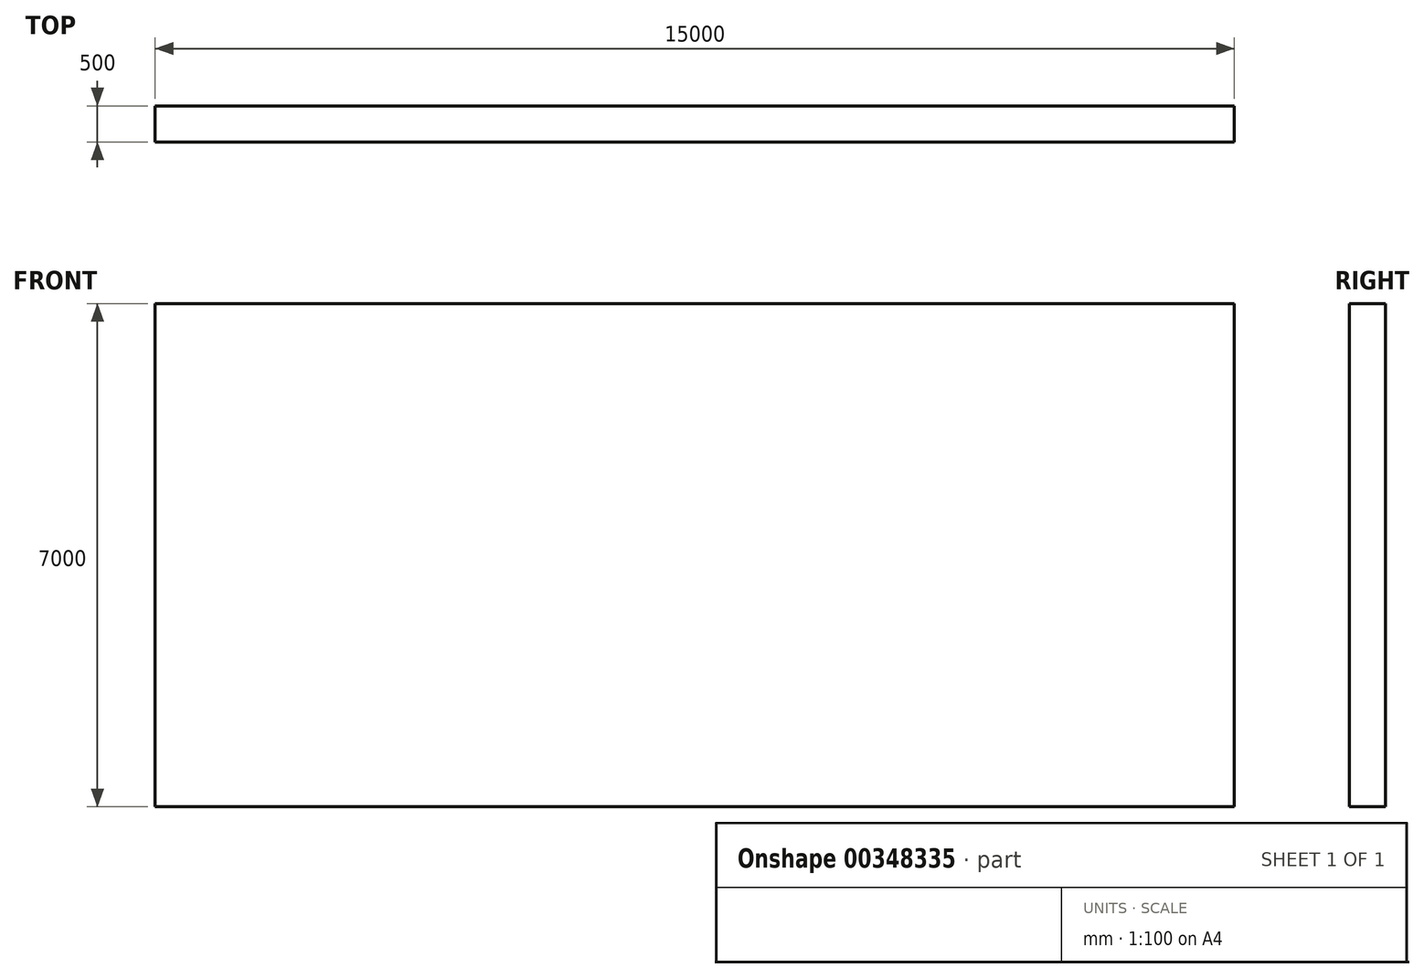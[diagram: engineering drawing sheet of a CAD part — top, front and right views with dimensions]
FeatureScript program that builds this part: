
annotation { "Feature Type Name" : "Feature", "Feature Type Description" : "" }
export const myFeature = defineFeature(function(context is Context, id is Id, definition is map)
    precondition{}
    {
        {
            var Q0;
            Q0=qCreatedBy(makeId("Front.planeOp"),FACE);
            var sketch = newSketch(context, id + "F0", { "sketchPlane" : qUnion([Q0])});
            skLineSegment(sketch, "E0.bottom", {"start": v(7500, 3500) * mm, "end": v(-7500, 3500) * mm});
            skLineSegment(sketch, "E0.top", {"start": v(7500, -3500) * mm, "end": v(-7500, -3500) * mm});
            skLineSegment(sketch, "E0.left", {"start": v(7500, 3500) * mm, "end": v(7500, -3500) * mm});
            skLineSegment(sketch, "E0.right", {"start": v(-7500, 3500) * mm, "end": v(-7500, -3500) * mm});
            skPoint(sketch, "E0.middle", {"position": v(0, 0) * mm});
            skSolve(sketch);
        }
        {
            var Q0;
            Q0=makeQuery(id+"F0.imprint","IMPRINT",FACE,{"disambiguationData":[TD([[makeQuery(id+"F0.imprint","IMPRINT",EDGE,{"derivedFrom":sQuery(id+"F0.wireOp",EDGE,"E0.bottom")}),1.0]])]});
            extrude(context, id + "F1", {"entities" : qUnion([Q0]), "depth" : 500 * mm});
        }
        {
            var Q0;
            Q0=makeQuery(id+"F1.opExtrude","CAP_FACE",FACE,{"disambiguationData":[OSD([sQuery(id+"F0.wireOp",EDGE,"E0.bottom"),sQuery(id+"F0.wireOp",EDGE,"E0.top"),sQuery(id+"F0.wireOp",EDGE,"E0.left"),sQuery(id+"F0.wireOp",EDGE,"E0.right")])],"isStart":false});
            var sketch = newSketch(context, id + "F2", { "sketchPlane" : qUnion([Q0])});
            skLineSegment(sketch, "E1.MirrorCS", {"start": v(-7500, -3000) * mm, "end": v(7500, -3000) * mm});
            skLineSegment(sketch, "E2", {"start": v(7500, -3500) * mm, "end": v(-7500, -3500) * mm});
            skLineSegment(sketch, "E3.MirrorCS", {"start": v(-1000, -3500) * mm, "end": v(-1000, 3500) * mm});
            skLineSegment(sketch, "E4.0", {"start": v(-7490, -3500) * mm, "end": v(-7490, 3500) * mm});
            skLineSegment(sketch, "E5.0", {"start": v(-6990, -3500) * mm, "end": v(-6990, 3500) * mm});
            skLineSegment(sketch, "E6.MirrorCS", {"start": v(-7010, -3500) * mm, "end": v(-7010, 3500) * mm});
            skLineSegment(sketch, "E7.0", {"start": v(-6490, -3500) * mm, "end": v(-6490, 3500) * mm});
            skLineSegment(sketch, "E8.MirrorCS", {"start": v(-6510, -3500) * mm, "end": v(-6510, 3500) * mm});
            skLineSegment(sketch, "E9.0", {"start": v(-5990, -3500) * mm, "end": v(-5990, 3500) * mm});
            skLineSegment(sketch, "E10.MirrorCS", {"start": v(-6010, -3500) * mm, "end": v(-6010, 3500) * mm});
            skLineSegment(sketch, "E11.0", {"start": v(-5490, -3500) * mm, "end": v(-5490, 3500) * mm});
            skLineSegment(sketch, "E12.MirrorCS", {"start": v(-5510, -3500) * mm, "end": v(-5510, 3500) * mm});
            skLineSegment(sketch, "E13.0", {"start": v(-4990, -3500) * mm, "end": v(-4990, 3500) * mm});
            skLineSegment(sketch, "E14.MirrorCS", {"start": v(-5010, -3500) * mm, "end": v(-5010, 3500) * mm});
            skLineSegment(sketch, "E15.0", {"start": v(-4490, -3500) * mm, "end": v(-4490, 3500) * mm});
            skLineSegment(sketch, "E16.MirrorCS", {"start": v(-4510, -3500) * mm, "end": v(-4510, 3500) * mm});
            skLineSegment(sketch, "E17.0", {"start": v(-3990, -3500) * mm, "end": v(-3990, 3500) * mm});
            skLineSegment(sketch, "E18.MirrorCS", {"start": v(-4010, -3500) * mm, "end": v(-4010, 3500) * mm});
            skLineSegment(sketch, "E19.0", {"start": v(-3490, -3500) * mm, "end": v(-3490, 3500) * mm});
            skLineSegment(sketch, "E20.MirrorCS", {"start": v(-3510, -3500) * mm, "end": v(-3510, 3500) * mm});
            skLineSegment(sketch, "E21.0", {"start": v(-2990, -3500) * mm, "end": v(-2990, 3500) * mm});
            skLineSegment(sketch, "E22.MirrorCS", {"start": v(-3010, -3500) * mm, "end": v(-3010, 3500) * mm});
            skLineSegment(sketch, "E23.0", {"start": v(-2490, -3500) * mm, "end": v(-2490, 3500) * mm});
            skLineSegment(sketch, "E24.MirrorCS", {"start": v(-2510, -3500) * mm, "end": v(-2510, 3500) * mm});
            skLineSegment(sketch, "E25.0", {"start": v(-1990, -3500) * mm, "end": v(-1990, 3500) * mm});
            skLineSegment(sketch, "E26.MirrorCS", {"start": v(-2010, -3500) * mm, "end": v(-2010, 3500) * mm});
            skLineSegment(sketch, "E27.0", {"start": v(-1490, -3500) * mm, "end": v(-1490, 3500) * mm});
            skLineSegment(sketch, "E28.MirrorCS", {"start": v(-1510, -3500) * mm, "end": v(-1510, 3500) * mm});
            skLineSegment(sketch, "E29.MirrorCS", {"start": v(-510, -3500) * mm, "end": v(-510, 3500) * mm});
            skLineSegment(sketch, "E30.MirrorCS", {"start": v(-490, -3500) * mm, "end": v(-490, 3500) * mm});
            skLineSegment(sketch, "E31.MirrorCS", {"start": v(-10, -3500) * mm, "end": v(-10, 3500) * mm});
            skLineSegment(sketch, "E32.MirrorCS", {"start": v(10, -3500) * mm, "end": v(10, 3500) * mm});
            skLineSegment(sketch, "E33.MirrorCS", {"start": v(490, -3500) * mm, "end": v(490, 3500) * mm});
            skLineSegment(sketch, "E34.MirrorCS", {"start": v(510, -3500) * mm, "end": v(510, 3500) * mm});
            skLineSegment(sketch, "E35.MirrorCS", {"start": v(990, -3500) * mm, "end": v(990, 3500) * mm});
            skLineSegment(sketch, "E36.MirrorCS", {"start": v(1010, -3500) * mm, "end": v(1010, 3500) * mm});
            skLineSegment(sketch, "E37.MirrorCS", {"start": v(1490, -3500) * mm, "end": v(1490, 3500) * mm});
            skLineSegment(sketch, "E38.MirrorCS", {"start": v(1510, -3500) * mm, "end": v(1510, 3500) * mm});
            skLineSegment(sketch, "E39.MirrorCS", {"start": v(1990, -3500) * mm, "end": v(1990, 3500) * mm});
            skLineSegment(sketch, "E40.MirrorCS", {"start": v(2010, -3500) * mm, "end": v(2010, 3500) * mm});
            skLineSegment(sketch, "E41.MirrorCS", {"start": v(2490, -3500) * mm, "end": v(2490, 3500) * mm});
            skLineSegment(sketch, "E42.MirrorCS", {"start": v(2510, -3500) * mm, "end": v(2510, 3500) * mm});
            skLineSegment(sketch, "E43.MirrorCS", {"start": v(2990, -3500) * mm, "end": v(2990, 3500) * mm});
            skLineSegment(sketch, "E44.MirrorCS", {"start": v(3010, -3500) * mm, "end": v(3010, 3500) * mm});
            skLineSegment(sketch, "E45.MirrorCS", {"start": v(-980, -3500) * mm, "end": v(-980, 3500) * mm});
            skLineSegment(sketch, "E46.MirrorCS", {"start": v(3990, -3500) * mm, "end": v(3990, 3500) * mm});
            skLineSegment(sketch, "E47.MirrorCS", {"start": v(4010, -3500) * mm, "end": v(4010, 3500) * mm});
            skLineSegment(sketch, "E48.MirrorCS", {"start": v(4490, -3500) * mm, "end": v(4490, 3500) * mm});
            skLineSegment(sketch, "E49.MirrorCS", {"start": v(4510, -3500) * mm, "end": v(4510, 3500) * mm});
            skLineSegment(sketch, "E50.MirrorCS", {"start": v(4990, -3500) * mm, "end": v(4990, 3500) * mm});
            skLineSegment(sketch, "E51.MirrorCS", {"start": v(5010, -3500) * mm, "end": v(5010, 3500) * mm});
            skLineSegment(sketch, "E52.MirrorCS", {"start": v(5490, -3500) * mm, "end": v(5490, 3500) * mm});
            skLineSegment(sketch, "E53.MirrorCS", {"start": v(5510, -3500) * mm, "end": v(5510, 3500) * mm});
            skLineSegment(sketch, "E54.MirrorCS", {"start": v(5990, -3500) * mm, "end": v(5990, 3500) * mm});
            skLineSegment(sketch, "E55.MirrorCS", {"start": v(6010, -3500) * mm, "end": v(6010, 3500) * mm});
            skLineSegment(sketch, "E56.MirrorCS", {"start": v(6490, -3500) * mm, "end": v(6490, 3500) * mm});
            skLineSegment(sketch, "E57.MirrorCS", {"start": v(6510, -3500) * mm, "end": v(6510, 3500) * mm});
            skLineSegment(sketch, "E58.MirrorCS", {"start": v(6990, -3500) * mm, "end": v(6990, 3500) * mm});
            skLineSegment(sketch, "E59.MirrorCS", {"start": v(7010, -3500) * mm, "end": v(7010, 3500) * mm});
            skLineSegment(sketch, "E60.0", {"start": v(7490, 3500) * mm, "end": v(7490, -3500) * mm});
            skLineSegment(sketch, "E61.0", {"start": v(3510, -3500) * mm, "end": v(3510, 3500) * mm});
            skLineSegment(sketch, "E62.MirrorCS", {"start": v(3490, -3500) * mm, "end": v(3490, 3500) * mm});
            skLineSegment(sketch, "E63.0", {"start": v(-7500, 3490) * mm, "end": v(7500, 3490) * mm});
            skLineSegment(sketch, "E64.0", {"start": v(-7500, 3004.6) * mm, "end": v(7500, 3004.6) * mm});
            skLineSegment(sketch, "E65.MirrorCS", {"start": v(-7500, 3024.6) * mm, "end": v(7500, 3024.6) * mm});
            skLineSegment(sketch, "E66.MirrorCS", {"start": v(-7500, 2024.6) * mm, "end": v(7500, 2024.6) * mm});
            skLineSegment(sketch, "E67.MirrorCS", {"start": v(-7500, 1997.3) * mm, "end": v(7500, 1997.3) * mm});
            skLineSegment(sketch, "E68.0", {"start": v(-7500, 2500.95) * mm, "end": v(7500, 2500.95) * mm});
            skLineSegment(sketch, "E69.MirrorCS", {"start": v(-7500, 2520.95) * mm, "end": v(7500, 2520.95) * mm});
            skLineSegment(sketch, "E70.MirrorCS", {"start": v(-7500, 1017.3) * mm, "end": v(7500, 1017.3) * mm});
            skLineSegment(sketch, "E71.MirrorCS", {"start": v(-7500, 997.3) * mm, "end": v(7500, 997.3) * mm});
            skLineSegment(sketch, "E72.MirrorCS", {"start": v(-7500, 513.65) * mm, "end": v(7500, 513.65) * mm});
            skLineSegment(sketch, "E73.MirrorCS", {"start": v(-7500, 493.65) * mm, "end": v(7500, 493.65) * mm});
            skLineSegment(sketch, "E74.MirrorCS", {"start": v(-7500, 10) * mm, "end": v(7500, 10) * mm});
            skLineSegment(sketch, "E75.MirrorCS", {"start": v(-7500, -10) * mm, "end": v(7500, -10) * mm});
            skLineSegment(sketch, "E76.0", {"start": v(-7500, 1500.95) * mm, "end": v(7500, 1500.95) * mm});
            skLineSegment(sketch, "E77.MirrorCS", {"start": v(-7500, 1520.95) * mm, "end": v(7500, 1520.95) * mm});
            skLineSegment(sketch, "E78.MirrorCS", {"start": v(-7500, -982.7) * mm, "end": v(7500, -982.7) * mm});
            skLineSegment(sketch, "E79.MirrorCS", {"start": v(-7500, -1002.7) * mm, "end": v(7500, -1002.7) * mm});
            skLineSegment(sketch, "E80.MirrorCS", {"start": v(-7500, -1486.35) * mm, "end": v(7500, -1486.35) * mm});
            skLineSegment(sketch, "E81.MirrorCS", {"start": v(-7500, -1506.35) * mm, "end": v(7500, -1506.35) * mm});
            skLineSegment(sketch, "E82.MirrorCS", {"start": v(-7500, -1990) * mm, "end": v(7500, -1990) * mm});
            skLineSegment(sketch, "E83.MirrorCS", {"start": v(-7500, -2010) * mm, "end": v(7500, -2010) * mm});
            skLineSegment(sketch, "E84.MirrorCS", {"start": v(-7500, -2493.65) * mm, "end": v(7500, -2493.65) * mm});
            skLineSegment(sketch, "E85.MirrorCS", {"start": v(-7500, -2513.65) * mm, "end": v(7500, -2513.65) * mm});
            skLineSegment(sketch, "E86.MirrorCS", {"start": v(-7500, -3017.3) * mm, "end": v(7500, -3017.3) * mm});
            skLineSegment(sketch, "E87.0", {"start": v(-7500, -506.35) * mm, "end": v(7500, -506.35) * mm});
            skLineSegment(sketch, "E88.MirrorCS", {"start": v(-7500, -486.35) * mm, "end": v(7500, -486.35) * mm});
            skSolve(sketch);
        }
        {
            var Q0;
            {var subQ0=sQuery(id+"F2.wireOp",EDGE,"E65.MirrorCS");var subQ1=sQuery(id+"F2.wireOp",EDGE,"E4.0");var subQ2=makeQuery(id+"F2.imprint","INTERSECT",VERTEX,{"derivedFrom":[subQ1,subQ0]});Q0=makeQuery(id+"F2.imprint","IMPRINT",FACE,{"disambiguationData":[TD([[makeQuery(id+"F2.imprint","IMPRINT",EDGE,{"disambiguationData":[TD([[subQ2,-1.0]])],"derivedFrom":subQ1}),-1.0]])]});}
            var Q1;
            {var subQ0=sQuery(id+"F2.wireOp",EDGE,"E69.MirrorCS");var subQ1=sQuery(id+"F2.wireOp",EDGE,"E4.0");var subQ2=makeQuery(id+"F2.imprint","INTERSECT",VERTEX,{"derivedFrom":[subQ1,subQ0]});Q1=makeQuery(id+"F2.imprint","IMPRINT",FACE,{"disambiguationData":[TD([[makeQuery(id+"F2.imprint","IMPRINT",EDGE,{"disambiguationData":[TD([[subQ2,-1.0]])],"derivedFrom":subQ1}),-1.0]])]});}
            var Q2;
            {var subQ0=sQuery(id+"F2.wireOp",EDGE,"E66.MirrorCS");var subQ1=sQuery(id+"F2.wireOp",EDGE,"E4.0");var subQ2=makeQuery(id+"F2.imprint","INTERSECT",VERTEX,{"derivedFrom":[subQ1,subQ0]});Q2=makeQuery(id+"F2.imprint","IMPRINT",FACE,{"disambiguationData":[TD([[makeQuery(id+"F2.imprint","IMPRINT",EDGE,{"disambiguationData":[TD([[subQ2,-1.0]])],"derivedFrom":subQ1}),-1.0]])]});}
            var Q3;
            {var subQ0=sQuery(id+"F2.wireOp",EDGE,"E77.MirrorCS");var subQ1=sQuery(id+"F2.wireOp",EDGE,"E4.0");var subQ2=makeQuery(id+"F2.imprint","INTERSECT",VERTEX,{"derivedFrom":[subQ1,subQ0]});Q3=makeQuery(id+"F2.imprint","IMPRINT",FACE,{"disambiguationData":[TD([[makeQuery(id+"F2.imprint","IMPRINT",EDGE,{"disambiguationData":[TD([[subQ2,-1.0]])],"derivedFrom":subQ1}),-1.0]])]});}
            var Q4;
            {var subQ0=sQuery(id+"F2.wireOp",EDGE,"E70.MirrorCS");var subQ1=sQuery(id+"F2.wireOp",EDGE,"E4.0");var subQ2=makeQuery(id+"F2.imprint","INTERSECT",VERTEX,{"derivedFrom":[subQ1,subQ0]});Q4=makeQuery(id+"F2.imprint","IMPRINT",FACE,{"disambiguationData":[TD([[makeQuery(id+"F2.imprint","IMPRINT",EDGE,{"disambiguationData":[TD([[subQ2,-1.0]])],"derivedFrom":subQ1}),-1.0]])]});}
            var Q5;
            {var subQ0=sQuery(id+"F2.wireOp",EDGE,"E72.MirrorCS");var subQ1=sQuery(id+"F2.wireOp",EDGE,"E4.0");var subQ2=makeQuery(id+"F2.imprint","INTERSECT",VERTEX,{"derivedFrom":[subQ1,subQ0]});Q5=makeQuery(id+"F2.imprint","IMPRINT",FACE,{"disambiguationData":[TD([[makeQuery(id+"F2.imprint","IMPRINT",EDGE,{"disambiguationData":[TD([[subQ2,-1.0]])],"derivedFrom":subQ1}),-1.0]])]});}
            var Q6;
            {var subQ0=sQuery(id+"F2.wireOp",EDGE,"E74.MirrorCS");var subQ1=sQuery(id+"F2.wireOp",EDGE,"E4.0");var subQ2=makeQuery(id+"F2.imprint","INTERSECT",VERTEX,{"derivedFrom":[subQ1,subQ0]});Q6=makeQuery(id+"F2.imprint","IMPRINT",FACE,{"disambiguationData":[TD([[makeQuery(id+"F2.imprint","IMPRINT",EDGE,{"disambiguationData":[TD([[subQ2,-1.0]])],"derivedFrom":subQ1}),-1.0]])]});}
            var Q7;
            {var subQ0=sQuery(id+"F2.wireOp",EDGE,"E88.MirrorCS");var subQ1=sQuery(id+"F2.wireOp",EDGE,"E4.0");var subQ2=makeQuery(id+"F2.imprint","INTERSECT",VERTEX,{"derivedFrom":[subQ1,subQ0]});Q7=makeQuery(id+"F2.imprint","IMPRINT",FACE,{"disambiguationData":[TD([[makeQuery(id+"F2.imprint","IMPRINT",EDGE,{"disambiguationData":[TD([[subQ2,-1.0]])],"derivedFrom":subQ1}),-1.0]])]});}
            var Q8;
            {var subQ0=sQuery(id+"F2.wireOp",EDGE,"E78.MirrorCS");var subQ1=sQuery(id+"F2.wireOp",EDGE,"E4.0");var subQ2=makeQuery(id+"F2.imprint","INTERSECT",VERTEX,{"derivedFrom":[subQ1,subQ0]});Q8=makeQuery(id+"F2.imprint","IMPRINT",FACE,{"disambiguationData":[TD([[makeQuery(id+"F2.imprint","IMPRINT",EDGE,{"disambiguationData":[TD([[subQ2,-1.0]])],"derivedFrom":subQ1}),-1.0]])]});}
            var Q9;
            {var subQ0=sQuery(id+"F2.wireOp",EDGE,"E80.MirrorCS");var subQ1=sQuery(id+"F2.wireOp",EDGE,"E4.0");var subQ2=makeQuery(id+"F2.imprint","INTERSECT",VERTEX,{"derivedFrom":[subQ1,subQ0]});Q9=makeQuery(id+"F2.imprint","IMPRINT",FACE,{"disambiguationData":[TD([[makeQuery(id+"F2.imprint","IMPRINT",EDGE,{"disambiguationData":[TD([[subQ2,-1.0]])],"derivedFrom":subQ1}),-1.0]])]});}
            var Q10;
            {var subQ0=sQuery(id+"F2.wireOp",EDGE,"E82.MirrorCS");var subQ1=sQuery(id+"F2.wireOp",EDGE,"E4.0");var subQ2=makeQuery(id+"F2.imprint","INTERSECT",VERTEX,{"derivedFrom":[subQ1,subQ0]});Q10=makeQuery(id+"F2.imprint","IMPRINT",FACE,{"disambiguationData":[TD([[makeQuery(id+"F2.imprint","IMPRINT",EDGE,{"disambiguationData":[TD([[subQ2,-1.0]])],"derivedFrom":subQ1}),-1.0]])]});}
            var Q11;
            {var subQ0=sQuery(id+"F2.wireOp",EDGE,"E84.MirrorCS");var subQ1=sQuery(id+"F2.wireOp",EDGE,"E4.0");var subQ2=makeQuery(id+"F2.imprint","INTERSECT",VERTEX,{"derivedFrom":[subQ1,subQ0]});Q11=makeQuery(id+"F2.imprint","IMPRINT",FACE,{"disambiguationData":[TD([[makeQuery(id+"F2.imprint","IMPRINT",EDGE,{"disambiguationData":[TD([[subQ2,-1.0]])],"derivedFrom":subQ1}),-1.0]])]});}
            var Q12;
            {var subQ0=sQuery(id+"F2.wireOp",EDGE,"E4.0");var subQ1=sQuery(id+"F2.wireOp",EDGE,"E1.MirrorCS");var subQ2=makeQuery(id+"F2.imprint","INTERSECT",VERTEX,{"derivedFrom":[subQ1,subQ0]});Q12=makeQuery(id+"F2.imprint","IMPRINT",FACE,{"disambiguationData":[TD([[makeQuery(id+"F2.imprint","IMPRINT",EDGE,{"disambiguationData":[TD([[subQ2,-1.0]])],"derivedFrom":subQ1}),1.0]])]});}
            var Q13;
            {var subQ0=sQuery(id+"F2.wireOp",EDGE,"E4.0");var subQ1=sQuery(id+"F2.wireOp",EDGE,"E2");var subQ2=makeQuery(id+"F2.imprint","INTERSECT",VERTEX,{"derivedFrom":[subQ1,subQ0]});Q13=makeQuery(id+"F2.imprint","IMPRINT",FACE,{"disambiguationData":[TD([[makeQuery(id+"F2.imprint","IMPRINT",EDGE,{"disambiguationData":[TD([[subQ2,1.0]])],"derivedFrom":subQ1}),-1.0]])]});}
            var Q14;
            {var subQ0=sQuery(id+"F2.wireOp",EDGE,"E5.0");var subQ1=sQuery(id+"F2.wireOp",EDGE,"E2");var subQ2=makeQuery(id+"F2.imprint","INTERSECT",VERTEX,{"derivedFrom":[subQ1,subQ0]});Q14=makeQuery(id+"F2.imprint","IMPRINT",FACE,{"disambiguationData":[TD([[makeQuery(id+"F2.imprint","IMPRINT",EDGE,{"disambiguationData":[TD([[subQ2,1.0]])],"derivedFrom":subQ1}),-1.0]])]});}
            var Q15;
            {var subQ0=sQuery(id+"F2.wireOp",EDGE,"E5.0");var subQ1=sQuery(id+"F2.wireOp",EDGE,"E1.MirrorCS");var subQ2=makeQuery(id+"F2.imprint","INTERSECT",VERTEX,{"derivedFrom":[subQ1,subQ0]});Q15=makeQuery(id+"F2.imprint","IMPRINT",FACE,{"disambiguationData":[TD([[makeQuery(id+"F2.imprint","IMPRINT",EDGE,{"disambiguationData":[TD([[subQ2,-1.0]])],"derivedFrom":subQ1}),1.0]])]});}
            var Q16;
            {var subQ0=sQuery(id+"F2.wireOp",EDGE,"E84.MirrorCS");var subQ1=sQuery(id+"F2.wireOp",EDGE,"E5.0");var subQ2=makeQuery(id+"F2.imprint","INTERSECT",VERTEX,{"derivedFrom":[subQ1,subQ0]});Q16=makeQuery(id+"F2.imprint","IMPRINT",FACE,{"disambiguationData":[TD([[makeQuery(id+"F2.imprint","IMPRINT",EDGE,{"disambiguationData":[TD([[subQ2,-1.0]])],"derivedFrom":subQ1}),-1.0]])]});}
            var Q17;
            {var subQ0=sQuery(id+"F2.wireOp",EDGE,"E82.MirrorCS");var subQ1=sQuery(id+"F2.wireOp",EDGE,"E5.0");var subQ2=makeQuery(id+"F2.imprint","INTERSECT",VERTEX,{"derivedFrom":[subQ1,subQ0]});Q17=makeQuery(id+"F2.imprint","IMPRINT",FACE,{"disambiguationData":[TD([[makeQuery(id+"F2.imprint","IMPRINT",EDGE,{"disambiguationData":[TD([[subQ2,-1.0]])],"derivedFrom":subQ1}),-1.0]])]});}
            var Q18;
            {var subQ0=sQuery(id+"F2.wireOp",EDGE,"E80.MirrorCS");var subQ1=sQuery(id+"F2.wireOp",EDGE,"E5.0");var subQ2=makeQuery(id+"F2.imprint","INTERSECT",VERTEX,{"derivedFrom":[subQ1,subQ0]});Q18=makeQuery(id+"F2.imprint","IMPRINT",FACE,{"disambiguationData":[TD([[makeQuery(id+"F2.imprint","IMPRINT",EDGE,{"disambiguationData":[TD([[subQ2,-1.0]])],"derivedFrom":subQ1}),-1.0]])]});}
            var Q19;
            {var subQ0=sQuery(id+"F2.wireOp",EDGE,"E78.MirrorCS");var subQ1=sQuery(id+"F2.wireOp",EDGE,"E5.0");var subQ2=makeQuery(id+"F2.imprint","INTERSECT",VERTEX,{"derivedFrom":[subQ1,subQ0]});Q19=makeQuery(id+"F2.imprint","IMPRINT",FACE,{"disambiguationData":[TD([[makeQuery(id+"F2.imprint","IMPRINT",EDGE,{"disambiguationData":[TD([[subQ2,-1.0]])],"derivedFrom":subQ1}),-1.0]])]});}
            var Q20;
            {var subQ0=sQuery(id+"F2.wireOp",EDGE,"E88.MirrorCS");var subQ1=sQuery(id+"F2.wireOp",EDGE,"E5.0");var subQ2=makeQuery(id+"F2.imprint","INTERSECT",VERTEX,{"derivedFrom":[subQ1,subQ0]});Q20=makeQuery(id+"F2.imprint","IMPRINT",FACE,{"disambiguationData":[TD([[makeQuery(id+"F2.imprint","IMPRINT",EDGE,{"disambiguationData":[TD([[subQ2,-1.0]])],"derivedFrom":subQ1}),-1.0]])]});}
            var Q21;
            {var subQ0=sQuery(id+"F2.wireOp",EDGE,"E74.MirrorCS");var subQ1=sQuery(id+"F2.wireOp",EDGE,"E5.0");var subQ2=makeQuery(id+"F2.imprint","INTERSECT",VERTEX,{"derivedFrom":[subQ1,subQ0]});Q21=makeQuery(id+"F2.imprint","IMPRINT",FACE,{"disambiguationData":[TD([[makeQuery(id+"F2.imprint","IMPRINT",EDGE,{"disambiguationData":[TD([[subQ2,-1.0]])],"derivedFrom":subQ1}),-1.0]])]});}
            var Q22;
            {var subQ0=sQuery(id+"F2.wireOp",EDGE,"E72.MirrorCS");var subQ1=sQuery(id+"F2.wireOp",EDGE,"E5.0");var subQ2=makeQuery(id+"F2.imprint","INTERSECT",VERTEX,{"derivedFrom":[subQ1,subQ0]});Q22=makeQuery(id+"F2.imprint","IMPRINT",FACE,{"disambiguationData":[TD([[makeQuery(id+"F2.imprint","IMPRINT",EDGE,{"disambiguationData":[TD([[subQ2,-1.0]])],"derivedFrom":subQ1}),-1.0]])]});}
            var Q23;
            {var subQ0=sQuery(id+"F2.wireOp",EDGE,"E70.MirrorCS");var subQ1=sQuery(id+"F2.wireOp",EDGE,"E5.0");var subQ2=makeQuery(id+"F2.imprint","INTERSECT",VERTEX,{"derivedFrom":[subQ1,subQ0]});Q23=makeQuery(id+"F2.imprint","IMPRINT",FACE,{"disambiguationData":[TD([[makeQuery(id+"F2.imprint","IMPRINT",EDGE,{"disambiguationData":[TD([[subQ2,-1.0]])],"derivedFrom":subQ1}),-1.0]])]});}
            var Q24;
            {var subQ0=sQuery(id+"F2.wireOp",EDGE,"E77.MirrorCS");var subQ1=sQuery(id+"F2.wireOp",EDGE,"E5.0");var subQ2=makeQuery(id+"F2.imprint","INTERSECT",VERTEX,{"derivedFrom":[subQ1,subQ0]});Q24=makeQuery(id+"F2.imprint","IMPRINT",FACE,{"disambiguationData":[TD([[makeQuery(id+"F2.imprint","IMPRINT",EDGE,{"disambiguationData":[TD([[subQ2,-1.0]])],"derivedFrom":subQ1}),-1.0]])]});}
            var Q25;
            {var subQ0=sQuery(id+"F2.wireOp",EDGE,"E66.MirrorCS");var subQ1=sQuery(id+"F2.wireOp",EDGE,"E5.0");var subQ2=makeQuery(id+"F2.imprint","INTERSECT",VERTEX,{"derivedFrom":[subQ1,subQ0]});Q25=makeQuery(id+"F2.imprint","IMPRINT",FACE,{"disambiguationData":[TD([[makeQuery(id+"F2.imprint","IMPRINT",EDGE,{"disambiguationData":[TD([[subQ2,-1.0]])],"derivedFrom":subQ1}),-1.0]])]});}
            var Q26;
            {var subQ0=sQuery(id+"F2.wireOp",EDGE,"E69.MirrorCS");var subQ1=sQuery(id+"F2.wireOp",EDGE,"E5.0");var subQ2=makeQuery(id+"F2.imprint","INTERSECT",VERTEX,{"derivedFrom":[subQ1,subQ0]});Q26=makeQuery(id+"F2.imprint","IMPRINT",FACE,{"disambiguationData":[TD([[makeQuery(id+"F2.imprint","IMPRINT",EDGE,{"disambiguationData":[TD([[subQ2,-1.0]])],"derivedFrom":subQ1}),-1.0]])]});}
            var Q27;
            {var subQ0=sQuery(id+"F2.wireOp",EDGE,"E65.MirrorCS");var subQ1=sQuery(id+"F2.wireOp",EDGE,"E7.0");var subQ2=makeQuery(id+"F2.imprint","INTERSECT",VERTEX,{"derivedFrom":[subQ1,subQ0]});Q27=makeQuery(id+"F2.imprint","IMPRINT",FACE,{"disambiguationData":[TD([[makeQuery(id+"F2.imprint","IMPRINT",EDGE,{"disambiguationData":[TD([[subQ2,-1.0]])],"derivedFrom":subQ1}),-1.0]])]});}
            var Q28;
            {var subQ0=sQuery(id+"F2.wireOp",EDGE,"E69.MirrorCS");var subQ1=sQuery(id+"F2.wireOp",EDGE,"E7.0");var subQ2=makeQuery(id+"F2.imprint","INTERSECT",VERTEX,{"derivedFrom":[subQ1,subQ0]});Q28=makeQuery(id+"F2.imprint","IMPRINT",FACE,{"disambiguationData":[TD([[makeQuery(id+"F2.imprint","IMPRINT",EDGE,{"disambiguationData":[TD([[subQ2,-1.0]])],"derivedFrom":subQ1}),-1.0]])]});}
            var Q29;
            {var subQ0=sQuery(id+"F2.wireOp",EDGE,"E66.MirrorCS");var subQ1=sQuery(id+"F2.wireOp",EDGE,"E7.0");var subQ2=makeQuery(id+"F2.imprint","INTERSECT",VERTEX,{"derivedFrom":[subQ1,subQ0]});Q29=makeQuery(id+"F2.imprint","IMPRINT",FACE,{"disambiguationData":[TD([[makeQuery(id+"F2.imprint","IMPRINT",EDGE,{"disambiguationData":[TD([[subQ2,-1.0]])],"derivedFrom":subQ1}),-1.0]])]});}
            var Q30;
            {var subQ0=sQuery(id+"F2.wireOp",EDGE,"E77.MirrorCS");var subQ1=sQuery(id+"F2.wireOp",EDGE,"E7.0");var subQ2=makeQuery(id+"F2.imprint","INTERSECT",VERTEX,{"derivedFrom":[subQ1,subQ0]});Q30=makeQuery(id+"F2.imprint","IMPRINT",FACE,{"disambiguationData":[TD([[makeQuery(id+"F2.imprint","IMPRINT",EDGE,{"disambiguationData":[TD([[subQ2,-1.0]])],"derivedFrom":subQ1}),-1.0]])]});}
            var Q31;
            {var subQ0=sQuery(id+"F2.wireOp",EDGE,"E70.MirrorCS");var subQ1=sQuery(id+"F2.wireOp",EDGE,"E7.0");var subQ2=makeQuery(id+"F2.imprint","INTERSECT",VERTEX,{"derivedFrom":[subQ1,subQ0]});Q31=makeQuery(id+"F2.imprint","IMPRINT",FACE,{"disambiguationData":[TD([[makeQuery(id+"F2.imprint","IMPRINT",EDGE,{"disambiguationData":[TD([[subQ2,-1.0]])],"derivedFrom":subQ1}),-1.0]])]});}
            var Q32;
            {var subQ0=sQuery(id+"F2.wireOp",EDGE,"E72.MirrorCS");var subQ1=sQuery(id+"F2.wireOp",EDGE,"E7.0");var subQ2=makeQuery(id+"F2.imprint","INTERSECT",VERTEX,{"derivedFrom":[subQ1,subQ0]});Q32=makeQuery(id+"F2.imprint","IMPRINT",FACE,{"disambiguationData":[TD([[makeQuery(id+"F2.imprint","IMPRINT",EDGE,{"disambiguationData":[TD([[subQ2,-1.0]])],"derivedFrom":subQ1}),-1.0]])]});}
            var Q33;
            {var subQ0=sQuery(id+"F2.wireOp",EDGE,"E74.MirrorCS");var subQ1=sQuery(id+"F2.wireOp",EDGE,"E7.0");var subQ2=makeQuery(id+"F2.imprint","INTERSECT",VERTEX,{"derivedFrom":[subQ1,subQ0]});Q33=makeQuery(id+"F2.imprint","IMPRINT",FACE,{"disambiguationData":[TD([[makeQuery(id+"F2.imprint","IMPRINT",EDGE,{"disambiguationData":[TD([[subQ2,-1.0]])],"derivedFrom":subQ1}),-1.0]])]});}
            var Q34;
            {var subQ0=sQuery(id+"F2.wireOp",EDGE,"E88.MirrorCS");var subQ1=sQuery(id+"F2.wireOp",EDGE,"E7.0");var subQ2=makeQuery(id+"F2.imprint","INTERSECT",VERTEX,{"derivedFrom":[subQ1,subQ0]});Q34=makeQuery(id+"F2.imprint","IMPRINT",FACE,{"disambiguationData":[TD([[makeQuery(id+"F2.imprint","IMPRINT",EDGE,{"disambiguationData":[TD([[subQ2,-1.0]])],"derivedFrom":subQ1}),-1.0]])]});}
            var Q35;
            {var subQ0=sQuery(id+"F2.wireOp",EDGE,"E88.MirrorCS");var subQ1=sQuery(id+"F2.wireOp",EDGE,"E30.MirrorCS");var subQ2=makeQuery(id+"F2.imprint","INTERSECT",VERTEX,{"derivedFrom":[subQ1,subQ0]});Q35=makeQuery(id+"F2.imprint","IMPRINT",FACE,{"disambiguationData":[TD([[makeQuery(id+"F2.imprint","IMPRINT",EDGE,{"disambiguationData":[TD([[subQ2,-1.0]])],"derivedFrom":subQ1}),-1.0]])]});}
            var Q36;
            {var subQ0=sQuery(id+"F2.wireOp",EDGE,"E88.MirrorCS");var subQ1=sQuery(id+"F2.wireOp",EDGE,"E32.MirrorCS");var subQ2=makeQuery(id+"F2.imprint","INTERSECT",VERTEX,{"derivedFrom":[subQ1,subQ0]});Q36=makeQuery(id+"F2.imprint","IMPRINT",FACE,{"disambiguationData":[TD([[makeQuery(id+"F2.imprint","IMPRINT",EDGE,{"disambiguationData":[TD([[subQ2,-1.0]])],"derivedFrom":subQ1}),-1.0]])]});}
            var Q37;
            {var subQ0=sQuery(id+"F2.wireOp",EDGE,"E74.MirrorCS");var subQ1=sQuery(id+"F2.wireOp",EDGE,"E32.MirrorCS");var subQ2=makeQuery(id+"F2.imprint","INTERSECT",VERTEX,{"derivedFrom":[subQ1,subQ0]});Q37=makeQuery(id+"F2.imprint","IMPRINT",FACE,{"disambiguationData":[TD([[makeQuery(id+"F2.imprint","IMPRINT",EDGE,{"disambiguationData":[TD([[subQ2,-1.0]])],"derivedFrom":subQ1}),-1.0]])]});}
            var Q38;
            {var subQ0=sQuery(id+"F2.wireOp",EDGE,"E74.MirrorCS");var subQ1=sQuery(id+"F2.wireOp",EDGE,"E30.MirrorCS");var subQ2=makeQuery(id+"F2.imprint","INTERSECT",VERTEX,{"derivedFrom":[subQ1,subQ0]});Q38=makeQuery(id+"F2.imprint","IMPRINT",FACE,{"disambiguationData":[TD([[makeQuery(id+"F2.imprint","IMPRINT",EDGE,{"disambiguationData":[TD([[subQ2,-1.0]])],"derivedFrom":subQ1}),-1.0]])]});}
            var Q39;
            {var subQ0=sQuery(id+"F2.wireOp",EDGE,"E78.MirrorCS");var subQ1=sQuery(id+"F2.wireOp",EDGE,"E7.0");var subQ2=makeQuery(id+"F2.imprint","INTERSECT",VERTEX,{"derivedFrom":[subQ1,subQ0]});Q39=makeQuery(id+"F2.imprint","IMPRINT",FACE,{"disambiguationData":[TD([[makeQuery(id+"F2.imprint","IMPRINT",EDGE,{"disambiguationData":[TD([[subQ2,-1.0]])],"derivedFrom":subQ1}),-1.0]])]});}
            var Q40;
            {var subQ0=sQuery(id+"F2.wireOp",EDGE,"E80.MirrorCS");var subQ1=sQuery(id+"F2.wireOp",EDGE,"E7.0");var subQ2=makeQuery(id+"F2.imprint","INTERSECT",VERTEX,{"derivedFrom":[subQ1,subQ0]});Q40=makeQuery(id+"F2.imprint","IMPRINT",FACE,{"disambiguationData":[TD([[makeQuery(id+"F2.imprint","IMPRINT",EDGE,{"disambiguationData":[TD([[subQ2,-1.0]])],"derivedFrom":subQ1}),-1.0]])]});}
            var Q41;
            {var subQ0=sQuery(id+"F2.wireOp",EDGE,"E82.MirrorCS");var subQ1=sQuery(id+"F2.wireOp",EDGE,"E7.0");var subQ2=makeQuery(id+"F2.imprint","INTERSECT",VERTEX,{"derivedFrom":[subQ1,subQ0]});Q41=makeQuery(id+"F2.imprint","IMPRINT",FACE,{"disambiguationData":[TD([[makeQuery(id+"F2.imprint","IMPRINT",EDGE,{"disambiguationData":[TD([[subQ2,-1.0]])],"derivedFrom":subQ1}),-1.0]])]});}
            var Q42;
            {var subQ0=sQuery(id+"F2.wireOp",EDGE,"E84.MirrorCS");var subQ1=sQuery(id+"F2.wireOp",EDGE,"E7.0");var subQ2=makeQuery(id+"F2.imprint","INTERSECT",VERTEX,{"derivedFrom":[subQ1,subQ0]});Q42=makeQuery(id+"F2.imprint","IMPRINT",FACE,{"disambiguationData":[TD([[makeQuery(id+"F2.imprint","IMPRINT",EDGE,{"disambiguationData":[TD([[subQ2,-1.0]])],"derivedFrom":subQ1}),-1.0]])]});}
            var Q43;
            {var subQ0=sQuery(id+"F2.wireOp",EDGE,"E7.0");var subQ1=sQuery(id+"F2.wireOp",EDGE,"E1.MirrorCS");var subQ2=makeQuery(id+"F2.imprint","INTERSECT",VERTEX,{"derivedFrom":[subQ1,subQ0]});Q43=makeQuery(id+"F2.imprint","IMPRINT",FACE,{"disambiguationData":[TD([[makeQuery(id+"F2.imprint","IMPRINT",EDGE,{"disambiguationData":[TD([[subQ2,-1.0]])],"derivedFrom":subQ1}),1.0]])]});}
            var Q44;
            {var subQ0=sQuery(id+"F2.wireOp",EDGE,"E7.0");var subQ1=sQuery(id+"F2.wireOp",EDGE,"E2");var subQ2=makeQuery(id+"F2.imprint","INTERSECT",VERTEX,{"derivedFrom":[subQ1,subQ0]});Q44=makeQuery(id+"F2.imprint","IMPRINT",FACE,{"disambiguationData":[TD([[makeQuery(id+"F2.imprint","IMPRINT",EDGE,{"disambiguationData":[TD([[subQ2,1.0]])],"derivedFrom":subQ1}),-1.0]])]});}
            var Q45;
            {var subQ0=sQuery(id+"F2.wireOp",EDGE,"E9.0");var subQ1=sQuery(id+"F2.wireOp",EDGE,"E2");var subQ2=makeQuery(id+"F2.imprint","INTERSECT",VERTEX,{"derivedFrom":[subQ1,subQ0]});Q45=makeQuery(id+"F2.imprint","IMPRINT",FACE,{"disambiguationData":[TD([[makeQuery(id+"F2.imprint","IMPRINT",EDGE,{"disambiguationData":[TD([[subQ2,1.0]])],"derivedFrom":subQ1}),-1.0]])]});}
            var Q46;
            {var subQ0=sQuery(id+"F2.wireOp",EDGE,"E9.0");var subQ1=sQuery(id+"F2.wireOp",EDGE,"E1.MirrorCS");var subQ2=makeQuery(id+"F2.imprint","INTERSECT",VERTEX,{"derivedFrom":[subQ1,subQ0]});Q46=makeQuery(id+"F2.imprint","IMPRINT",FACE,{"disambiguationData":[TD([[makeQuery(id+"F2.imprint","IMPRINT",EDGE,{"disambiguationData":[TD([[subQ2,-1.0]])],"derivedFrom":subQ1}),1.0]])]});}
            var Q47;
            {var subQ0=sQuery(id+"F2.wireOp",EDGE,"E84.MirrorCS");var subQ1=sQuery(id+"F2.wireOp",EDGE,"E9.0");var subQ2=makeQuery(id+"F2.imprint","INTERSECT",VERTEX,{"derivedFrom":[subQ1,subQ0]});Q47=makeQuery(id+"F2.imprint","IMPRINT",FACE,{"disambiguationData":[TD([[makeQuery(id+"F2.imprint","IMPRINT",EDGE,{"disambiguationData":[TD([[subQ2,-1.0]])],"derivedFrom":subQ1}),-1.0]])]});}
            var Q48;
            {var subQ0=sQuery(id+"F2.wireOp",EDGE,"E82.MirrorCS");var subQ1=sQuery(id+"F2.wireOp",EDGE,"E9.0");var subQ2=makeQuery(id+"F2.imprint","INTERSECT",VERTEX,{"derivedFrom":[subQ1,subQ0]});Q48=makeQuery(id+"F2.imprint","IMPRINT",FACE,{"disambiguationData":[TD([[makeQuery(id+"F2.imprint","IMPRINT",EDGE,{"disambiguationData":[TD([[subQ2,-1.0]])],"derivedFrom":subQ1}),-1.0]])]});}
            var Q49;
            {var subQ0=sQuery(id+"F2.wireOp",EDGE,"E80.MirrorCS");var subQ1=sQuery(id+"F2.wireOp",EDGE,"E9.0");var subQ2=makeQuery(id+"F2.imprint","INTERSECT",VERTEX,{"derivedFrom":[subQ1,subQ0]});Q49=makeQuery(id+"F2.imprint","IMPRINT",FACE,{"disambiguationData":[TD([[makeQuery(id+"F2.imprint","IMPRINT",EDGE,{"disambiguationData":[TD([[subQ2,-1.0]])],"derivedFrom":subQ1}),-1.0]])]});}
            var Q50;
            {var subQ0=sQuery(id+"F2.wireOp",EDGE,"E78.MirrorCS");var subQ1=sQuery(id+"F2.wireOp",EDGE,"E9.0");var subQ2=makeQuery(id+"F2.imprint","INTERSECT",VERTEX,{"derivedFrom":[subQ1,subQ0]});Q50=makeQuery(id+"F2.imprint","IMPRINT",FACE,{"disambiguationData":[TD([[makeQuery(id+"F2.imprint","IMPRINT",EDGE,{"disambiguationData":[TD([[subQ2,-1.0]])],"derivedFrom":subQ1}),-1.0]])]});}
            var Q51;
            {var subQ0=sQuery(id+"F2.wireOp",EDGE,"E88.MirrorCS");var subQ1=sQuery(id+"F2.wireOp",EDGE,"E9.0");var subQ2=makeQuery(id+"F2.imprint","INTERSECT",VERTEX,{"derivedFrom":[subQ1,subQ0]});Q51=makeQuery(id+"F2.imprint","IMPRINT",FACE,{"disambiguationData":[TD([[makeQuery(id+"F2.imprint","IMPRINT",EDGE,{"disambiguationData":[TD([[subQ2,-1.0]])],"derivedFrom":subQ1}),-1.0]])]});}
            var Q52;
            {var subQ0=sQuery(id+"F2.wireOp",EDGE,"E74.MirrorCS");var subQ1=sQuery(id+"F2.wireOp",EDGE,"E9.0");var subQ2=makeQuery(id+"F2.imprint","INTERSECT",VERTEX,{"derivedFrom":[subQ1,subQ0]});Q52=makeQuery(id+"F2.imprint","IMPRINT",FACE,{"disambiguationData":[TD([[makeQuery(id+"F2.imprint","IMPRINT",EDGE,{"disambiguationData":[TD([[subQ2,-1.0]])],"derivedFrom":subQ1}),-1.0]])]});}
            var Q53;
            {var subQ0=sQuery(id+"F2.wireOp",EDGE,"E72.MirrorCS");var subQ1=sQuery(id+"F2.wireOp",EDGE,"E9.0");var subQ2=makeQuery(id+"F2.imprint","INTERSECT",VERTEX,{"derivedFrom":[subQ1,subQ0]});Q53=makeQuery(id+"F2.imprint","IMPRINT",FACE,{"disambiguationData":[TD([[makeQuery(id+"F2.imprint","IMPRINT",EDGE,{"disambiguationData":[TD([[subQ2,-1.0]])],"derivedFrom":subQ1}),-1.0]])]});}
            var Q54;
            {var subQ0=sQuery(id+"F2.wireOp",EDGE,"E70.MirrorCS");var subQ1=sQuery(id+"F2.wireOp",EDGE,"E9.0");var subQ2=makeQuery(id+"F2.imprint","INTERSECT",VERTEX,{"derivedFrom":[subQ1,subQ0]});Q54=makeQuery(id+"F2.imprint","IMPRINT",FACE,{"disambiguationData":[TD([[makeQuery(id+"F2.imprint","IMPRINT",EDGE,{"disambiguationData":[TD([[subQ2,-1.0]])],"derivedFrom":subQ1}),-1.0]])]});}
            var Q55;
            {var subQ0=sQuery(id+"F2.wireOp",EDGE,"E77.MirrorCS");var subQ1=sQuery(id+"F2.wireOp",EDGE,"E9.0");var subQ2=makeQuery(id+"F2.imprint","INTERSECT",VERTEX,{"derivedFrom":[subQ1,subQ0]});Q55=makeQuery(id+"F2.imprint","IMPRINT",FACE,{"disambiguationData":[TD([[makeQuery(id+"F2.imprint","IMPRINT",EDGE,{"disambiguationData":[TD([[subQ2,-1.0]])],"derivedFrom":subQ1}),-1.0]])]});}
            var Q56;
            {var subQ0=sQuery(id+"F2.wireOp",EDGE,"E66.MirrorCS");var subQ1=sQuery(id+"F2.wireOp",EDGE,"E9.0");var subQ2=makeQuery(id+"F2.imprint","INTERSECT",VERTEX,{"derivedFrom":[subQ1,subQ0]});Q56=makeQuery(id+"F2.imprint","IMPRINT",FACE,{"disambiguationData":[TD([[makeQuery(id+"F2.imprint","IMPRINT",EDGE,{"disambiguationData":[TD([[subQ2,-1.0]])],"derivedFrom":subQ1}),-1.0]])]});}
            var Q57;
            {var subQ0=sQuery(id+"F2.wireOp",EDGE,"E69.MirrorCS");var subQ1=sQuery(id+"F2.wireOp",EDGE,"E9.0");var subQ2=makeQuery(id+"F2.imprint","INTERSECT",VERTEX,{"derivedFrom":[subQ1,subQ0]});Q57=makeQuery(id+"F2.imprint","IMPRINT",FACE,{"disambiguationData":[TD([[makeQuery(id+"F2.imprint","IMPRINT",EDGE,{"disambiguationData":[TD([[subQ2,-1.0]])],"derivedFrom":subQ1}),-1.0]])]});}
            var Q58;
            {var subQ0=sQuery(id+"F2.wireOp",EDGE,"E65.MirrorCS");var subQ1=sQuery(id+"F2.wireOp",EDGE,"E9.0");var subQ2=makeQuery(id+"F2.imprint","INTERSECT",VERTEX,{"derivedFrom":[subQ1,subQ0]});Q58=makeQuery(id+"F2.imprint","IMPRINT",FACE,{"disambiguationData":[TD([[makeQuery(id+"F2.imprint","IMPRINT",EDGE,{"disambiguationData":[TD([[subQ2,-1.0]])],"derivedFrom":subQ1}),-1.0]])]});}
            var Q59;
            {var subQ0=sQuery(id+"F2.wireOp",EDGE,"E65.MirrorCS");var subQ1=sQuery(id+"F2.wireOp",EDGE,"E5.0");var subQ2=makeQuery(id+"F2.imprint","INTERSECT",VERTEX,{"derivedFrom":[subQ1,subQ0]});Q59=makeQuery(id+"F2.imprint","IMPRINT",FACE,{"disambiguationData":[TD([[makeQuery(id+"F2.imprint","IMPRINT",EDGE,{"disambiguationData":[TD([[subQ2,-1.0]])],"derivedFrom":subQ1}),-1.0]])]});}
            var Q60;
            {var subQ0=sQuery(id+"F2.wireOp",EDGE,"E65.MirrorCS");var subQ1=sQuery(id+"F2.wireOp",EDGE,"E11.0");var subQ2=makeQuery(id+"F2.imprint","INTERSECT",VERTEX,{"derivedFrom":[subQ1,subQ0]});Q60=makeQuery(id+"F2.imprint","IMPRINT",FACE,{"disambiguationData":[TD([[makeQuery(id+"F2.imprint","IMPRINT",EDGE,{"disambiguationData":[TD([[subQ2,-1.0]])],"derivedFrom":subQ1}),-1.0]])]});}
            var Q61;
            {var subQ0=sQuery(id+"F2.wireOp",EDGE,"E69.MirrorCS");var subQ1=sQuery(id+"F2.wireOp",EDGE,"E11.0");var subQ2=makeQuery(id+"F2.imprint","INTERSECT",VERTEX,{"derivedFrom":[subQ1,subQ0]});Q61=makeQuery(id+"F2.imprint","IMPRINT",FACE,{"disambiguationData":[TD([[makeQuery(id+"F2.imprint","IMPRINT",EDGE,{"disambiguationData":[TD([[subQ2,-1.0]])],"derivedFrom":subQ1}),-1.0]])]});}
            var Q62;
            {var subQ0=sQuery(id+"F2.wireOp",EDGE,"E66.MirrorCS");var subQ1=sQuery(id+"F2.wireOp",EDGE,"E11.0");var subQ2=makeQuery(id+"F2.imprint","INTERSECT",VERTEX,{"derivedFrom":[subQ1,subQ0]});Q62=makeQuery(id+"F2.imprint","IMPRINT",FACE,{"disambiguationData":[TD([[makeQuery(id+"F2.imprint","IMPRINT",EDGE,{"disambiguationData":[TD([[subQ2,-1.0]])],"derivedFrom":subQ1}),-1.0]])]});}
            var Q63;
            {var subQ0=sQuery(id+"F2.wireOp",EDGE,"E77.MirrorCS");var subQ1=sQuery(id+"F2.wireOp",EDGE,"E11.0");var subQ2=makeQuery(id+"F2.imprint","INTERSECT",VERTEX,{"derivedFrom":[subQ1,subQ0]});Q63=makeQuery(id+"F2.imprint","IMPRINT",FACE,{"disambiguationData":[TD([[makeQuery(id+"F2.imprint","IMPRINT",EDGE,{"disambiguationData":[TD([[subQ2,-1.0]])],"derivedFrom":subQ1}),-1.0]])]});}
            var Q64;
            {var subQ0=sQuery(id+"F2.wireOp",EDGE,"E70.MirrorCS");var subQ1=sQuery(id+"F2.wireOp",EDGE,"E11.0");var subQ2=makeQuery(id+"F2.imprint","INTERSECT",VERTEX,{"derivedFrom":[subQ1,subQ0]});Q64=makeQuery(id+"F2.imprint","IMPRINT",FACE,{"disambiguationData":[TD([[makeQuery(id+"F2.imprint","IMPRINT",EDGE,{"disambiguationData":[TD([[subQ2,-1.0]])],"derivedFrom":subQ1}),-1.0]])]});}
            var Q65;
            {var subQ0=sQuery(id+"F2.wireOp",EDGE,"E72.MirrorCS");var subQ1=sQuery(id+"F2.wireOp",EDGE,"E11.0");var subQ2=makeQuery(id+"F2.imprint","INTERSECT",VERTEX,{"derivedFrom":[subQ1,subQ0]});Q65=makeQuery(id+"F2.imprint","IMPRINT",FACE,{"disambiguationData":[TD([[makeQuery(id+"F2.imprint","IMPRINT",EDGE,{"disambiguationData":[TD([[subQ2,-1.0]])],"derivedFrom":subQ1}),-1.0]])]});}
            var Q66;
            {var subQ0=sQuery(id+"F2.wireOp",EDGE,"E74.MirrorCS");var subQ1=sQuery(id+"F2.wireOp",EDGE,"E11.0");var subQ2=makeQuery(id+"F2.imprint","INTERSECT",VERTEX,{"derivedFrom":[subQ1,subQ0]});Q66=makeQuery(id+"F2.imprint","IMPRINT",FACE,{"disambiguationData":[TD([[makeQuery(id+"F2.imprint","IMPRINT",EDGE,{"disambiguationData":[TD([[subQ2,-1.0]])],"derivedFrom":subQ1}),-1.0]])]});}
            var Q67;
            {var subQ0=sQuery(id+"F2.wireOp",EDGE,"E88.MirrorCS");var subQ1=sQuery(id+"F2.wireOp",EDGE,"E11.0");var subQ2=makeQuery(id+"F2.imprint","INTERSECT",VERTEX,{"derivedFrom":[subQ1,subQ0]});Q67=makeQuery(id+"F2.imprint","IMPRINT",FACE,{"disambiguationData":[TD([[makeQuery(id+"F2.imprint","IMPRINT",EDGE,{"disambiguationData":[TD([[subQ2,-1.0]])],"derivedFrom":subQ1}),-1.0]])]});}
            var Q68;
            {var subQ0=sQuery(id+"F2.wireOp",EDGE,"E78.MirrorCS");var subQ1=sQuery(id+"F2.wireOp",EDGE,"E11.0");var subQ2=makeQuery(id+"F2.imprint","INTERSECT",VERTEX,{"derivedFrom":[subQ1,subQ0]});Q68=makeQuery(id+"F2.imprint","IMPRINT",FACE,{"disambiguationData":[TD([[makeQuery(id+"F2.imprint","IMPRINT",EDGE,{"disambiguationData":[TD([[subQ2,-1.0]])],"derivedFrom":subQ1}),-1.0]])]});}
            var Q69;
            {var subQ0=sQuery(id+"F2.wireOp",EDGE,"E80.MirrorCS");var subQ1=sQuery(id+"F2.wireOp",EDGE,"E11.0");var subQ2=makeQuery(id+"F2.imprint","INTERSECT",VERTEX,{"derivedFrom":[subQ1,subQ0]});Q69=makeQuery(id+"F2.imprint","IMPRINT",FACE,{"disambiguationData":[TD([[makeQuery(id+"F2.imprint","IMPRINT",EDGE,{"disambiguationData":[TD([[subQ2,-1.0]])],"derivedFrom":subQ1}),-1.0]])]});}
            var Q70;
            {var subQ0=sQuery(id+"F2.wireOp",EDGE,"E82.MirrorCS");var subQ1=sQuery(id+"F2.wireOp",EDGE,"E11.0");var subQ2=makeQuery(id+"F2.imprint","INTERSECT",VERTEX,{"derivedFrom":[subQ1,subQ0]});Q70=makeQuery(id+"F2.imprint","IMPRINT",FACE,{"disambiguationData":[TD([[makeQuery(id+"F2.imprint","IMPRINT",EDGE,{"disambiguationData":[TD([[subQ2,-1.0]])],"derivedFrom":subQ1}),-1.0]])]});}
            var Q71;
            {var subQ0=sQuery(id+"F2.wireOp",EDGE,"E84.MirrorCS");var subQ1=sQuery(id+"F2.wireOp",EDGE,"E11.0");var subQ2=makeQuery(id+"F2.imprint","INTERSECT",VERTEX,{"derivedFrom":[subQ1,subQ0]});Q71=makeQuery(id+"F2.imprint","IMPRINT",FACE,{"disambiguationData":[TD([[makeQuery(id+"F2.imprint","IMPRINT",EDGE,{"disambiguationData":[TD([[subQ2,-1.0]])],"derivedFrom":subQ1}),-1.0]])]});}
            var Q72;
            {var subQ0=sQuery(id+"F2.wireOp",EDGE,"E11.0");var subQ1=sQuery(id+"F2.wireOp",EDGE,"E1.MirrorCS");var subQ2=makeQuery(id+"F2.imprint","INTERSECT",VERTEX,{"derivedFrom":[subQ1,subQ0]});Q72=makeQuery(id+"F2.imprint","IMPRINT",FACE,{"disambiguationData":[TD([[makeQuery(id+"F2.imprint","IMPRINT",EDGE,{"disambiguationData":[TD([[subQ2,-1.0]])],"derivedFrom":subQ1}),1.0]])]});}
            var Q73;
            {var subQ0=sQuery(id+"F2.wireOp",EDGE,"E11.0");var subQ1=sQuery(id+"F2.wireOp",EDGE,"E2");var subQ2=makeQuery(id+"F2.imprint","INTERSECT",VERTEX,{"derivedFrom":[subQ1,subQ0]});Q73=makeQuery(id+"F2.imprint","IMPRINT",FACE,{"disambiguationData":[TD([[makeQuery(id+"F2.imprint","IMPRINT",EDGE,{"disambiguationData":[TD([[subQ2,1.0]])],"derivedFrom":subQ1}),-1.0]])]});}
            var Q74;
            {var subQ0=sQuery(id+"F2.wireOp",EDGE,"E13.0");var subQ1=sQuery(id+"F2.wireOp",EDGE,"E2");var subQ2=makeQuery(id+"F2.imprint","INTERSECT",VERTEX,{"derivedFrom":[subQ1,subQ0]});Q74=makeQuery(id+"F2.imprint","IMPRINT",FACE,{"disambiguationData":[TD([[makeQuery(id+"F2.imprint","IMPRINT",EDGE,{"disambiguationData":[TD([[subQ2,1.0]])],"derivedFrom":subQ1}),-1.0]])]});}
            var Q75;
            {var subQ0=sQuery(id+"F2.wireOp",EDGE,"E13.0");var subQ1=sQuery(id+"F2.wireOp",EDGE,"E1.MirrorCS");var subQ2=makeQuery(id+"F2.imprint","INTERSECT",VERTEX,{"derivedFrom":[subQ1,subQ0]});Q75=makeQuery(id+"F2.imprint","IMPRINT",FACE,{"disambiguationData":[TD([[makeQuery(id+"F2.imprint","IMPRINT",EDGE,{"disambiguationData":[TD([[subQ2,-1.0]])],"derivedFrom":subQ1}),1.0]])]});}
            var Q76;
            {var subQ0=sQuery(id+"F2.wireOp",EDGE,"E84.MirrorCS");var subQ1=sQuery(id+"F2.wireOp",EDGE,"E13.0");var subQ2=makeQuery(id+"F2.imprint","INTERSECT",VERTEX,{"derivedFrom":[subQ1,subQ0]});Q76=makeQuery(id+"F2.imprint","IMPRINT",FACE,{"disambiguationData":[TD([[makeQuery(id+"F2.imprint","IMPRINT",EDGE,{"disambiguationData":[TD([[subQ2,-1.0]])],"derivedFrom":subQ1}),-1.0]])]});}
            var Q77;
            {var subQ0=sQuery(id+"F2.wireOp",EDGE,"E82.MirrorCS");var subQ1=sQuery(id+"F2.wireOp",EDGE,"E13.0");var subQ2=makeQuery(id+"F2.imprint","INTERSECT",VERTEX,{"derivedFrom":[subQ1,subQ0]});Q77=makeQuery(id+"F2.imprint","IMPRINT",FACE,{"disambiguationData":[TD([[makeQuery(id+"F2.imprint","IMPRINT",EDGE,{"disambiguationData":[TD([[subQ2,-1.0]])],"derivedFrom":subQ1}),-1.0]])]});}
            var Q78;
            {var subQ0=sQuery(id+"F2.wireOp",EDGE,"E80.MirrorCS");var subQ1=sQuery(id+"F2.wireOp",EDGE,"E13.0");var subQ2=makeQuery(id+"F2.imprint","INTERSECT",VERTEX,{"derivedFrom":[subQ1,subQ0]});Q78=makeQuery(id+"F2.imprint","IMPRINT",FACE,{"disambiguationData":[TD([[makeQuery(id+"F2.imprint","IMPRINT",EDGE,{"disambiguationData":[TD([[subQ2,-1.0]])],"derivedFrom":subQ1}),-1.0]])]});}
            var Q79;
            {var subQ0=sQuery(id+"F2.wireOp",EDGE,"E78.MirrorCS");var subQ1=sQuery(id+"F2.wireOp",EDGE,"E13.0");var subQ2=makeQuery(id+"F2.imprint","INTERSECT",VERTEX,{"derivedFrom":[subQ1,subQ0]});Q79=makeQuery(id+"F2.imprint","IMPRINT",FACE,{"disambiguationData":[TD([[makeQuery(id+"F2.imprint","IMPRINT",EDGE,{"disambiguationData":[TD([[subQ2,-1.0]])],"derivedFrom":subQ1}),-1.0]])]});}
            var Q80;
            {var subQ0=sQuery(id+"F2.wireOp",EDGE,"E88.MirrorCS");var subQ1=sQuery(id+"F2.wireOp",EDGE,"E13.0");var subQ2=makeQuery(id+"F2.imprint","INTERSECT",VERTEX,{"derivedFrom":[subQ1,subQ0]});Q80=makeQuery(id+"F2.imprint","IMPRINT",FACE,{"disambiguationData":[TD([[makeQuery(id+"F2.imprint","IMPRINT",EDGE,{"disambiguationData":[TD([[subQ2,-1.0]])],"derivedFrom":subQ1}),-1.0]])]});}
            var Q81;
            {var subQ0=sQuery(id+"F2.wireOp",EDGE,"E74.MirrorCS");var subQ1=sQuery(id+"F2.wireOp",EDGE,"E13.0");var subQ2=makeQuery(id+"F2.imprint","INTERSECT",VERTEX,{"derivedFrom":[subQ1,subQ0]});Q81=makeQuery(id+"F2.imprint","IMPRINT",FACE,{"disambiguationData":[TD([[makeQuery(id+"F2.imprint","IMPRINT",EDGE,{"disambiguationData":[TD([[subQ2,-1.0]])],"derivedFrom":subQ1}),-1.0]])]});}
            var Q82;
            {var subQ0=sQuery(id+"F2.wireOp",EDGE,"E72.MirrorCS");var subQ1=sQuery(id+"F2.wireOp",EDGE,"E13.0");var subQ2=makeQuery(id+"F2.imprint","INTERSECT",VERTEX,{"derivedFrom":[subQ1,subQ0]});Q82=makeQuery(id+"F2.imprint","IMPRINT",FACE,{"disambiguationData":[TD([[makeQuery(id+"F2.imprint","IMPRINT",EDGE,{"disambiguationData":[TD([[subQ2,-1.0]])],"derivedFrom":subQ1}),-1.0]])]});}
            var Q83;
            {var subQ0=sQuery(id+"F2.wireOp",EDGE,"E70.MirrorCS");var subQ1=sQuery(id+"F2.wireOp",EDGE,"E13.0");var subQ2=makeQuery(id+"F2.imprint","INTERSECT",VERTEX,{"derivedFrom":[subQ1,subQ0]});Q83=makeQuery(id+"F2.imprint","IMPRINT",FACE,{"disambiguationData":[TD([[makeQuery(id+"F2.imprint","IMPRINT",EDGE,{"disambiguationData":[TD([[subQ2,-1.0]])],"derivedFrom":subQ1}),-1.0]])]});}
            var Q84;
            {var subQ0=sQuery(id+"F2.wireOp",EDGE,"E77.MirrorCS");var subQ1=sQuery(id+"F2.wireOp",EDGE,"E13.0");var subQ2=makeQuery(id+"F2.imprint","INTERSECT",VERTEX,{"derivedFrom":[subQ1,subQ0]});Q84=makeQuery(id+"F2.imprint","IMPRINT",FACE,{"disambiguationData":[TD([[makeQuery(id+"F2.imprint","IMPRINT",EDGE,{"disambiguationData":[TD([[subQ2,-1.0]])],"derivedFrom":subQ1}),-1.0]])]});}
            var Q85;
            {var subQ0=sQuery(id+"F2.wireOp",EDGE,"E66.MirrorCS");var subQ1=sQuery(id+"F2.wireOp",EDGE,"E13.0");var subQ2=makeQuery(id+"F2.imprint","INTERSECT",VERTEX,{"derivedFrom":[subQ1,subQ0]});Q85=makeQuery(id+"F2.imprint","IMPRINT",FACE,{"disambiguationData":[TD([[makeQuery(id+"F2.imprint","IMPRINT",EDGE,{"disambiguationData":[TD([[subQ2,-1.0]])],"derivedFrom":subQ1}),-1.0]])]});}
            var Q86;
            {var subQ0=sQuery(id+"F2.wireOp",EDGE,"E69.MirrorCS");var subQ1=sQuery(id+"F2.wireOp",EDGE,"E13.0");var subQ2=makeQuery(id+"F2.imprint","INTERSECT",VERTEX,{"derivedFrom":[subQ1,subQ0]});Q86=makeQuery(id+"F2.imprint","IMPRINT",FACE,{"disambiguationData":[TD([[makeQuery(id+"F2.imprint","IMPRINT",EDGE,{"disambiguationData":[TD([[subQ2,-1.0]])],"derivedFrom":subQ1}),-1.0]])]});}
            var Q87;
            {var subQ0=sQuery(id+"F2.wireOp",EDGE,"E65.MirrorCS");var subQ1=sQuery(id+"F2.wireOp",EDGE,"E13.0");var subQ2=makeQuery(id+"F2.imprint","INTERSECT",VERTEX,{"derivedFrom":[subQ1,subQ0]});Q87=makeQuery(id+"F2.imprint","IMPRINT",FACE,{"disambiguationData":[TD([[makeQuery(id+"F2.imprint","IMPRINT",EDGE,{"disambiguationData":[TD([[subQ2,-1.0]])],"derivedFrom":subQ1}),-1.0]])]});}
            var Q88;
            {var subQ0=sQuery(id+"F2.wireOp",EDGE,"E65.MirrorCS");var subQ1=sQuery(id+"F2.wireOp",EDGE,"E15.0");var subQ2=makeQuery(id+"F2.imprint","INTERSECT",VERTEX,{"derivedFrom":[subQ1,subQ0]});Q88=makeQuery(id+"F2.imprint","IMPRINT",FACE,{"disambiguationData":[TD([[makeQuery(id+"F2.imprint","IMPRINT",EDGE,{"disambiguationData":[TD([[subQ2,-1.0]])],"derivedFrom":subQ1}),-1.0]])]});}
            var Q89;
            {var subQ0=sQuery(id+"F2.wireOp",EDGE,"E69.MirrorCS");var subQ1=sQuery(id+"F2.wireOp",EDGE,"E15.0");var subQ2=makeQuery(id+"F2.imprint","INTERSECT",VERTEX,{"derivedFrom":[subQ1,subQ0]});Q89=makeQuery(id+"F2.imprint","IMPRINT",FACE,{"disambiguationData":[TD([[makeQuery(id+"F2.imprint","IMPRINT",EDGE,{"disambiguationData":[TD([[subQ2,-1.0]])],"derivedFrom":subQ1}),-1.0]])]});}
            var Q90;
            {var subQ0=sQuery(id+"F2.wireOp",EDGE,"E66.MirrorCS");var subQ1=sQuery(id+"F2.wireOp",EDGE,"E15.0");var subQ2=makeQuery(id+"F2.imprint","INTERSECT",VERTEX,{"derivedFrom":[subQ1,subQ0]});Q90=makeQuery(id+"F2.imprint","IMPRINT",FACE,{"disambiguationData":[TD([[makeQuery(id+"F2.imprint","IMPRINT",EDGE,{"disambiguationData":[TD([[subQ2,-1.0]])],"derivedFrom":subQ1}),-1.0]])]});}
            var Q91;
            {var subQ0=sQuery(id+"F2.wireOp",EDGE,"E77.MirrorCS");var subQ1=sQuery(id+"F2.wireOp",EDGE,"E15.0");var subQ2=makeQuery(id+"F2.imprint","INTERSECT",VERTEX,{"derivedFrom":[subQ1,subQ0]});Q91=makeQuery(id+"F2.imprint","IMPRINT",FACE,{"disambiguationData":[TD([[makeQuery(id+"F2.imprint","IMPRINT",EDGE,{"disambiguationData":[TD([[subQ2,-1.0]])],"derivedFrom":subQ1}),-1.0]])]});}
            var Q92;
            {var subQ0=sQuery(id+"F2.wireOp",EDGE,"E72.MirrorCS");var subQ1=sQuery(id+"F2.wireOp",EDGE,"E15.0");var subQ2=makeQuery(id+"F2.imprint","INTERSECT",VERTEX,{"derivedFrom":[subQ1,subQ0]});Q92=makeQuery(id+"F2.imprint","IMPRINT",FACE,{"disambiguationData":[TD([[makeQuery(id+"F2.imprint","IMPRINT",EDGE,{"disambiguationData":[TD([[subQ2,-1.0]])],"derivedFrom":subQ1}),-1.0]])]});}
            var Q93;
            {var subQ0=sQuery(id+"F2.wireOp",EDGE,"E74.MirrorCS");var subQ1=sQuery(id+"F2.wireOp",EDGE,"E15.0");var subQ2=makeQuery(id+"F2.imprint","INTERSECT",VERTEX,{"derivedFrom":[subQ1,subQ0]});Q93=makeQuery(id+"F2.imprint","IMPRINT",FACE,{"disambiguationData":[TD([[makeQuery(id+"F2.imprint","IMPRINT",EDGE,{"disambiguationData":[TD([[subQ2,-1.0]])],"derivedFrom":subQ1}),-1.0]])]});}
            var Q94;
            {var subQ0=sQuery(id+"F2.wireOp",EDGE,"E88.MirrorCS");var subQ1=sQuery(id+"F2.wireOp",EDGE,"E15.0");var subQ2=makeQuery(id+"F2.imprint","INTERSECT",VERTEX,{"derivedFrom":[subQ1,subQ0]});Q94=makeQuery(id+"F2.imprint","IMPRINT",FACE,{"disambiguationData":[TD([[makeQuery(id+"F2.imprint","IMPRINT",EDGE,{"disambiguationData":[TD([[subQ2,-1.0]])],"derivedFrom":subQ1}),-1.0]])]});}
            var Q95;
            {var subQ0=sQuery(id+"F2.wireOp",EDGE,"E78.MirrorCS");var subQ1=sQuery(id+"F2.wireOp",EDGE,"E15.0");var subQ2=makeQuery(id+"F2.imprint","INTERSECT",VERTEX,{"derivedFrom":[subQ1,subQ0]});Q95=makeQuery(id+"F2.imprint","IMPRINT",FACE,{"disambiguationData":[TD([[makeQuery(id+"F2.imprint","IMPRINT",EDGE,{"disambiguationData":[TD([[subQ2,-1.0]])],"derivedFrom":subQ1}),-1.0]])]});}
            var Q96;
            {var subQ0=sQuery(id+"F2.wireOp",EDGE,"E80.MirrorCS");var subQ1=sQuery(id+"F2.wireOp",EDGE,"E15.0");var subQ2=makeQuery(id+"F2.imprint","INTERSECT",VERTEX,{"derivedFrom":[subQ1,subQ0]});Q96=makeQuery(id+"F2.imprint","IMPRINT",FACE,{"disambiguationData":[TD([[makeQuery(id+"F2.imprint","IMPRINT",EDGE,{"disambiguationData":[TD([[subQ2,-1.0]])],"derivedFrom":subQ1}),-1.0]])]});}
            var Q97;
            {var subQ0=sQuery(id+"F2.wireOp",EDGE,"E82.MirrorCS");var subQ1=sQuery(id+"F2.wireOp",EDGE,"E15.0");var subQ2=makeQuery(id+"F2.imprint","INTERSECT",VERTEX,{"derivedFrom":[subQ1,subQ0]});Q97=makeQuery(id+"F2.imprint","IMPRINT",FACE,{"disambiguationData":[TD([[makeQuery(id+"F2.imprint","IMPRINT",EDGE,{"disambiguationData":[TD([[subQ2,-1.0]])],"derivedFrom":subQ1}),-1.0]])]});}
            var Q98;
            {var subQ0=sQuery(id+"F2.wireOp",EDGE,"E84.MirrorCS");var subQ1=sQuery(id+"F2.wireOp",EDGE,"E15.0");var subQ2=makeQuery(id+"F2.imprint","INTERSECT",VERTEX,{"derivedFrom":[subQ1,subQ0]});Q98=makeQuery(id+"F2.imprint","IMPRINT",FACE,{"disambiguationData":[TD([[makeQuery(id+"F2.imprint","IMPRINT",EDGE,{"disambiguationData":[TD([[subQ2,-1.0]])],"derivedFrom":subQ1}),-1.0]])]});}
            var Q99;
            {var subQ0=sQuery(id+"F2.wireOp",EDGE,"E15.0");var subQ1=sQuery(id+"F2.wireOp",EDGE,"E1.MirrorCS");var subQ2=makeQuery(id+"F2.imprint","INTERSECT",VERTEX,{"derivedFrom":[subQ1,subQ0]});Q99=makeQuery(id+"F2.imprint","IMPRINT",FACE,{"disambiguationData":[TD([[makeQuery(id+"F2.imprint","IMPRINT",EDGE,{"disambiguationData":[TD([[subQ2,-1.0]])],"derivedFrom":subQ1}),1.0]])]});}
            var Q100;
            {var subQ0=sQuery(id+"F2.wireOp",EDGE,"E84.MirrorCS");var subQ1=sQuery(id+"F2.wireOp",EDGE,"E15.0");var subQ2=makeQuery(id+"F2.imprint","INTERSECT",VERTEX,{"derivedFrom":[subQ1,subQ0]});Q100=makeQuery(id+"F2.imprint","IMPRINT",FACE,{"disambiguationData":[TD([[makeQuery(id+"F2.imprint","IMPRINT",EDGE,{"disambiguationData":[TD([[subQ2,-1.0]])],"derivedFrom":subQ1}),-1.0]])]});}
            var Q101;
            {var subQ0=sQuery(id+"F2.wireOp",EDGE,"E70.MirrorCS");var subQ1=sQuery(id+"F2.wireOp",EDGE,"E15.0");var subQ2=makeQuery(id+"F2.imprint","INTERSECT",VERTEX,{"derivedFrom":[subQ1,subQ0]});Q101=makeQuery(id+"F2.imprint","IMPRINT",FACE,{"disambiguationData":[TD([[makeQuery(id+"F2.imprint","IMPRINT",EDGE,{"disambiguationData":[TD([[subQ2,-1.0]])],"derivedFrom":subQ1}),-1.0]])]});}
            var Q102;
            {var subQ0=sQuery(id+"F2.wireOp",EDGE,"E70.MirrorCS");var subQ1=sQuery(id+"F2.wireOp",EDGE,"E17.0");var subQ2=makeQuery(id+"F2.imprint","INTERSECT",VERTEX,{"derivedFrom":[subQ1,subQ0]});Q102=makeQuery(id+"F2.imprint","IMPRINT",FACE,{"disambiguationData":[TD([[makeQuery(id+"F2.imprint","IMPRINT",EDGE,{"disambiguationData":[TD([[subQ2,-1.0]])],"derivedFrom":subQ1}),-1.0]])]});}
            var Q103;
            {var subQ0=sQuery(id+"F2.wireOp",EDGE,"E72.MirrorCS");var subQ1=sQuery(id+"F2.wireOp",EDGE,"E17.0");var subQ2=makeQuery(id+"F2.imprint","INTERSECT",VERTEX,{"derivedFrom":[subQ1,subQ0]});Q103=makeQuery(id+"F2.imprint","IMPRINT",FACE,{"disambiguationData":[TD([[makeQuery(id+"F2.imprint","IMPRINT",EDGE,{"disambiguationData":[TD([[subQ2,-1.0]])],"derivedFrom":subQ1}),-1.0]])]});}
            var Q104;
            {var subQ0=sQuery(id+"F2.wireOp",EDGE,"E74.MirrorCS");var subQ1=sQuery(id+"F2.wireOp",EDGE,"E17.0");var subQ2=makeQuery(id+"F2.imprint","INTERSECT",VERTEX,{"derivedFrom":[subQ1,subQ0]});Q104=makeQuery(id+"F2.imprint","IMPRINT",FACE,{"disambiguationData":[TD([[makeQuery(id+"F2.imprint","IMPRINT",EDGE,{"disambiguationData":[TD([[subQ2,-1.0]])],"derivedFrom":subQ1}),-1.0]])]});}
            var Q105;
            {var subQ0=sQuery(id+"F2.wireOp",EDGE,"E88.MirrorCS");var subQ1=sQuery(id+"F2.wireOp",EDGE,"E17.0");var subQ2=makeQuery(id+"F2.imprint","INTERSECT",VERTEX,{"derivedFrom":[subQ1,subQ0]});Q105=makeQuery(id+"F2.imprint","IMPRINT",FACE,{"disambiguationData":[TD([[makeQuery(id+"F2.imprint","IMPRINT",EDGE,{"disambiguationData":[TD([[subQ2,-1.0]])],"derivedFrom":subQ1}),-1.0]])]});}
            var Q106;
            {var subQ0=sQuery(id+"F2.wireOp",EDGE,"E78.MirrorCS");var subQ1=sQuery(id+"F2.wireOp",EDGE,"E17.0");var subQ2=makeQuery(id+"F2.imprint","INTERSECT",VERTEX,{"derivedFrom":[subQ1,subQ0]});Q106=makeQuery(id+"F2.imprint","IMPRINT",FACE,{"disambiguationData":[TD([[makeQuery(id+"F2.imprint","IMPRINT",EDGE,{"disambiguationData":[TD([[subQ2,-1.0]])],"derivedFrom":subQ1}),-1.0]])]});}
            var Q107;
            {var subQ0=sQuery(id+"F2.wireOp",EDGE,"E80.MirrorCS");var subQ1=sQuery(id+"F2.wireOp",EDGE,"E17.0");var subQ2=makeQuery(id+"F2.imprint","INTERSECT",VERTEX,{"derivedFrom":[subQ1,subQ0]});Q107=makeQuery(id+"F2.imprint","IMPRINT",FACE,{"disambiguationData":[TD([[makeQuery(id+"F2.imprint","IMPRINT",EDGE,{"disambiguationData":[TD([[subQ2,-1.0]])],"derivedFrom":subQ1}),-1.0]])]});}
            var Q108;
            {var subQ0=sQuery(id+"F2.wireOp",EDGE,"E88.MirrorCS");var subQ1=sQuery(id+"F2.wireOp",EDGE,"E17.0");var subQ2=makeQuery(id+"F2.imprint","INTERSECT",VERTEX,{"derivedFrom":[subQ1,subQ0]});Q108=makeQuery(id+"F2.imprint","IMPRINT",FACE,{"disambiguationData":[TD([[makeQuery(id+"F2.imprint","IMPRINT",EDGE,{"disambiguationData":[TD([[subQ2,-1.0]])],"derivedFrom":subQ1}),-1.0]])]});}
            var Q109;
            {var subQ0=sQuery(id+"F2.wireOp",EDGE,"E82.MirrorCS");var subQ1=sQuery(id+"F2.wireOp",EDGE,"E17.0");var subQ2=makeQuery(id+"F2.imprint","INTERSECT",VERTEX,{"derivedFrom":[subQ1,subQ0]});Q109=makeQuery(id+"F2.imprint","IMPRINT",FACE,{"disambiguationData":[TD([[makeQuery(id+"F2.imprint","IMPRINT",EDGE,{"disambiguationData":[TD([[subQ2,-1.0]])],"derivedFrom":subQ1}),-1.0]])]});}
            var Q110;
            {var subQ0=sQuery(id+"F2.wireOp",EDGE,"E84.MirrorCS");var subQ1=sQuery(id+"F2.wireOp",EDGE,"E17.0");var subQ2=makeQuery(id+"F2.imprint","INTERSECT",VERTEX,{"derivedFrom":[subQ1,subQ0]});Q110=makeQuery(id+"F2.imprint","IMPRINT",FACE,{"disambiguationData":[TD([[makeQuery(id+"F2.imprint","IMPRINT",EDGE,{"disambiguationData":[TD([[subQ2,-1.0]])],"derivedFrom":subQ1}),-1.0]])]});}
            var Q111;
            {var subQ0=sQuery(id+"F2.wireOp",EDGE,"E17.0");var subQ1=sQuery(id+"F2.wireOp",EDGE,"E1.MirrorCS");var subQ2=makeQuery(id+"F2.imprint","INTERSECT",VERTEX,{"derivedFrom":[subQ1,subQ0]});Q111=makeQuery(id+"F2.imprint","IMPRINT",FACE,{"disambiguationData":[TD([[makeQuery(id+"F2.imprint","IMPRINT",EDGE,{"disambiguationData":[TD([[subQ2,-1.0]])],"derivedFrom":subQ1}),1.0]])]});}
            var Q112;
            {var subQ0=sQuery(id+"F2.wireOp",EDGE,"E17.0");var subQ1=sQuery(id+"F2.wireOp",EDGE,"E2");var subQ2=makeQuery(id+"F2.imprint","INTERSECT",VERTEX,{"derivedFrom":[subQ1,subQ0]});Q112=makeQuery(id+"F2.imprint","IMPRINT",FACE,{"disambiguationData":[TD([[makeQuery(id+"F2.imprint","IMPRINT",EDGE,{"disambiguationData":[TD([[subQ2,1.0]])],"derivedFrom":subQ1}),-1.0]])]});}
            var Q113;
            {var subQ0=sQuery(id+"F2.wireOp",EDGE,"E19.0");var subQ1=sQuery(id+"F2.wireOp",EDGE,"E2");var subQ2=makeQuery(id+"F2.imprint","INTERSECT",VERTEX,{"derivedFrom":[subQ1,subQ0]});Q113=makeQuery(id+"F2.imprint","IMPRINT",FACE,{"disambiguationData":[TD([[makeQuery(id+"F2.imprint","IMPRINT",EDGE,{"disambiguationData":[TD([[subQ2,1.0]])],"derivedFrom":subQ1}),-1.0]])]});}
            var Q114;
            {var subQ0=sQuery(id+"F2.wireOp",EDGE,"E19.0");var subQ1=sQuery(id+"F2.wireOp",EDGE,"E1.MirrorCS");var subQ2=makeQuery(id+"F2.imprint","INTERSECT",VERTEX,{"derivedFrom":[subQ1,subQ0]});Q114=makeQuery(id+"F2.imprint","IMPRINT",FACE,{"disambiguationData":[TD([[makeQuery(id+"F2.imprint","IMPRINT",EDGE,{"disambiguationData":[TD([[subQ2,-1.0]])],"derivedFrom":subQ1}),1.0]])]});}
            var Q115;
            {var subQ0=sQuery(id+"F2.wireOp",EDGE,"E82.MirrorCS");var subQ1=sQuery(id+"F2.wireOp",EDGE,"E19.0");var subQ2=makeQuery(id+"F2.imprint","INTERSECT",VERTEX,{"derivedFrom":[subQ1,subQ0]});Q115=makeQuery(id+"F2.imprint","IMPRINT",FACE,{"disambiguationData":[TD([[makeQuery(id+"F2.imprint","IMPRINT",EDGE,{"disambiguationData":[TD([[subQ2,-1.0]])],"derivedFrom":subQ1}),-1.0]])]});}
            var Q116;
            {var subQ0=sQuery(id+"F2.wireOp",EDGE,"E78.MirrorCS");var subQ1=sQuery(id+"F2.wireOp",EDGE,"E19.0");var subQ2=makeQuery(id+"F2.imprint","INTERSECT",VERTEX,{"derivedFrom":[subQ1,subQ0]});Q116=makeQuery(id+"F2.imprint","IMPRINT",FACE,{"disambiguationData":[TD([[makeQuery(id+"F2.imprint","IMPRINT",EDGE,{"disambiguationData":[TD([[subQ2,-1.0]])],"derivedFrom":subQ1}),-1.0]])]});}
            var Q117;
            {var subQ0=sQuery(id+"F2.wireOp",EDGE,"E88.MirrorCS");var subQ1=sQuery(id+"F2.wireOp",EDGE,"E19.0");var subQ2=makeQuery(id+"F2.imprint","INTERSECT",VERTEX,{"derivedFrom":[subQ1,subQ0]});Q117=makeQuery(id+"F2.imprint","IMPRINT",FACE,{"disambiguationData":[TD([[makeQuery(id+"F2.imprint","IMPRINT",EDGE,{"disambiguationData":[TD([[subQ2,-1.0]])],"derivedFrom":subQ1}),-1.0]])]});}
            var Q118;
            {var subQ0=sQuery(id+"F2.wireOp",EDGE,"E74.MirrorCS");var subQ1=sQuery(id+"F2.wireOp",EDGE,"E19.0");var subQ2=makeQuery(id+"F2.imprint","INTERSECT",VERTEX,{"derivedFrom":[subQ1,subQ0]});Q118=makeQuery(id+"F2.imprint","IMPRINT",FACE,{"disambiguationData":[TD([[makeQuery(id+"F2.imprint","IMPRINT",EDGE,{"disambiguationData":[TD([[subQ2,-1.0]])],"derivedFrom":subQ1}),-1.0]])]});}
            var Q119;
            {var subQ0=sQuery(id+"F2.wireOp",EDGE,"E72.MirrorCS");var subQ1=sQuery(id+"F2.wireOp",EDGE,"E19.0");var subQ2=makeQuery(id+"F2.imprint","INTERSECT",VERTEX,{"derivedFrom":[subQ1,subQ0]});Q119=makeQuery(id+"F2.imprint","IMPRINT",FACE,{"disambiguationData":[TD([[makeQuery(id+"F2.imprint","IMPRINT",EDGE,{"disambiguationData":[TD([[subQ2,-1.0]])],"derivedFrom":subQ1}),-1.0]])]});}
            var Q120;
            {var subQ0=sQuery(id+"F2.wireOp",EDGE,"E70.MirrorCS");var subQ1=sQuery(id+"F2.wireOp",EDGE,"E19.0");var subQ2=makeQuery(id+"F2.imprint","INTERSECT",VERTEX,{"derivedFrom":[subQ1,subQ0]});Q120=makeQuery(id+"F2.imprint","IMPRINT",FACE,{"disambiguationData":[TD([[makeQuery(id+"F2.imprint","IMPRINT",EDGE,{"disambiguationData":[TD([[subQ2,-1.0]])],"derivedFrom":subQ1}),-1.0]])]});}
            var Q121;
            {var subQ0=sQuery(id+"F2.wireOp",EDGE,"E77.MirrorCS");var subQ1=sQuery(id+"F2.wireOp",EDGE,"E19.0");var subQ2=makeQuery(id+"F2.imprint","INTERSECT",VERTEX,{"derivedFrom":[subQ1,subQ0]});Q121=makeQuery(id+"F2.imprint","IMPRINT",FACE,{"disambiguationData":[TD([[makeQuery(id+"F2.imprint","IMPRINT",EDGE,{"disambiguationData":[TD([[subQ2,-1.0]])],"derivedFrom":subQ1}),-1.0]])]});}
            var Q122;
            {var subQ0=sQuery(id+"F2.wireOp",EDGE,"E66.MirrorCS");var subQ1=sQuery(id+"F2.wireOp",EDGE,"E17.0");var subQ2=makeQuery(id+"F2.imprint","INTERSECT",VERTEX,{"derivedFrom":[subQ1,subQ0]});Q122=makeQuery(id+"F2.imprint","IMPRINT",FACE,{"disambiguationData":[TD([[makeQuery(id+"F2.imprint","IMPRINT",EDGE,{"disambiguationData":[TD([[subQ2,-1.0]])],"derivedFrom":subQ1}),-1.0]])]});}
            var Q123;
            {var subQ0=sQuery(id+"F2.wireOp",EDGE,"E66.MirrorCS");var subQ1=sQuery(id+"F2.wireOp",EDGE,"E19.0");var subQ2=makeQuery(id+"F2.imprint","INTERSECT",VERTEX,{"derivedFrom":[subQ1,subQ0]});Q123=makeQuery(id+"F2.imprint","IMPRINT",FACE,{"disambiguationData":[TD([[makeQuery(id+"F2.imprint","IMPRINT",EDGE,{"disambiguationData":[TD([[subQ2,-1.0]])],"derivedFrom":subQ1}),-1.0]])]});}
            var Q124;
            {var subQ0=sQuery(id+"F2.wireOp",EDGE,"E69.MirrorCS");var subQ1=sQuery(id+"F2.wireOp",EDGE,"E19.0");var subQ2=makeQuery(id+"F2.imprint","INTERSECT",VERTEX,{"derivedFrom":[subQ1,subQ0]});Q124=makeQuery(id+"F2.imprint","IMPRINT",FACE,{"disambiguationData":[TD([[makeQuery(id+"F2.imprint","IMPRINT",EDGE,{"disambiguationData":[TD([[subQ2,-1.0]])],"derivedFrom":subQ1}),-1.0]])]});}
            var Q125;
            {var subQ0=sQuery(id+"F2.wireOp",EDGE,"E65.MirrorCS");var subQ1=sQuery(id+"F2.wireOp",EDGE,"E17.0");var subQ2=makeQuery(id+"F2.imprint","INTERSECT",VERTEX,{"derivedFrom":[subQ1,subQ0]});Q125=makeQuery(id+"F2.imprint","IMPRINT",FACE,{"disambiguationData":[TD([[makeQuery(id+"F2.imprint","IMPRINT",EDGE,{"disambiguationData":[TD([[subQ2,-1.0]])],"derivedFrom":subQ1}),-1.0]])]});}
            var Q126;
            {var subQ0=sQuery(id+"F2.wireOp",EDGE,"E65.MirrorCS");var subQ1=sQuery(id+"F2.wireOp",EDGE,"E19.0");var subQ2=makeQuery(id+"F2.imprint","INTERSECT",VERTEX,{"derivedFrom":[subQ1,subQ0]});Q126=makeQuery(id+"F2.imprint","IMPRINT",FACE,{"disambiguationData":[TD([[makeQuery(id+"F2.imprint","IMPRINT",EDGE,{"disambiguationData":[TD([[subQ2,-1.0]])],"derivedFrom":subQ1}),-1.0]])]});}
            var Q127;
            {var subQ0=sQuery(id+"F2.wireOp",EDGE,"E84.MirrorCS");var subQ1=sQuery(id+"F2.wireOp",EDGE,"E19.0");var subQ2=makeQuery(id+"F2.imprint","INTERSECT",VERTEX,{"derivedFrom":[subQ1,subQ0]});Q127=makeQuery(id+"F2.imprint","IMPRINT",FACE,{"disambiguationData":[TD([[makeQuery(id+"F2.imprint","IMPRINT",EDGE,{"disambiguationData":[TD([[subQ2,-1.0]])],"derivedFrom":subQ1}),-1.0]])]});}
            var Q128;
            {var subQ0=sQuery(id+"F2.wireOp",EDGE,"E80.MirrorCS");var subQ1=sQuery(id+"F2.wireOp",EDGE,"E19.0");var subQ2=makeQuery(id+"F2.imprint","INTERSECT",VERTEX,{"derivedFrom":[subQ1,subQ0]});Q128=makeQuery(id+"F2.imprint","IMPRINT",FACE,{"disambiguationData":[TD([[makeQuery(id+"F2.imprint","IMPRINT",EDGE,{"disambiguationData":[TD([[subQ2,-1.0]])],"derivedFrom":subQ1}),-1.0]])]});}
            var Q129;
            {var subQ0=sQuery(id+"F2.wireOp",EDGE,"E21.0");var subQ1=sQuery(id+"F2.wireOp",EDGE,"E2");var subQ2=makeQuery(id+"F2.imprint","INTERSECT",VERTEX,{"derivedFrom":[subQ1,subQ0]});Q129=makeQuery(id+"F2.imprint","IMPRINT",FACE,{"disambiguationData":[TD([[makeQuery(id+"F2.imprint","IMPRINT",EDGE,{"disambiguationData":[TD([[subQ2,1.0]])],"derivedFrom":subQ1}),-1.0]])]});}
            var Q130;
            {var subQ0=sQuery(id+"F2.wireOp",EDGE,"E21.0");var subQ1=sQuery(id+"F2.wireOp",EDGE,"E1.MirrorCS");var subQ2=makeQuery(id+"F2.imprint","INTERSECT",VERTEX,{"derivedFrom":[subQ1,subQ0]});Q130=makeQuery(id+"F2.imprint","IMPRINT",FACE,{"disambiguationData":[TD([[makeQuery(id+"F2.imprint","IMPRINT",EDGE,{"disambiguationData":[TD([[subQ2,-1.0]])],"derivedFrom":subQ1}),1.0]])]});}
            var Q131;
            {var subQ0=sQuery(id+"F2.wireOp",EDGE,"E84.MirrorCS");var subQ1=sQuery(id+"F2.wireOp",EDGE,"E21.0");var subQ2=makeQuery(id+"F2.imprint","INTERSECT",VERTEX,{"derivedFrom":[subQ1,subQ0]});Q131=makeQuery(id+"F2.imprint","IMPRINT",FACE,{"disambiguationData":[TD([[makeQuery(id+"F2.imprint","IMPRINT",EDGE,{"disambiguationData":[TD([[subQ2,-1.0]])],"derivedFrom":subQ1}),-1.0]])]});}
            var Q132;
            {var subQ0=sQuery(id+"F2.wireOp",EDGE,"E82.MirrorCS");var subQ1=sQuery(id+"F2.wireOp",EDGE,"E21.0");var subQ2=makeQuery(id+"F2.imprint","INTERSECT",VERTEX,{"derivedFrom":[subQ1,subQ0]});Q132=makeQuery(id+"F2.imprint","IMPRINT",FACE,{"disambiguationData":[TD([[makeQuery(id+"F2.imprint","IMPRINT",EDGE,{"disambiguationData":[TD([[subQ2,-1.0]])],"derivedFrom":subQ1}),-1.0]])]});}
            var Q133;
            {var subQ0=sQuery(id+"F2.wireOp",EDGE,"E80.MirrorCS");var subQ1=sQuery(id+"F2.wireOp",EDGE,"E21.0");var subQ2=makeQuery(id+"F2.imprint","INTERSECT",VERTEX,{"derivedFrom":[subQ1,subQ0]});Q133=makeQuery(id+"F2.imprint","IMPRINT",FACE,{"disambiguationData":[TD([[makeQuery(id+"F2.imprint","IMPRINT",EDGE,{"disambiguationData":[TD([[subQ2,-1.0]])],"derivedFrom":subQ1}),-1.0]])]});}
            var Q134;
            {var subQ0=sQuery(id+"F2.wireOp",EDGE,"E88.MirrorCS");var subQ1=sQuery(id+"F2.wireOp",EDGE,"E21.0");var subQ2=makeQuery(id+"F2.imprint","INTERSECT",VERTEX,{"derivedFrom":[subQ1,subQ0]});Q134=makeQuery(id+"F2.imprint","IMPRINT",FACE,{"disambiguationData":[TD([[makeQuery(id+"F2.imprint","IMPRINT",EDGE,{"disambiguationData":[TD([[subQ2,-1.0]])],"derivedFrom":subQ1}),-1.0]])]});}
            var Q135;
            {var subQ0=sQuery(id+"F2.wireOp",EDGE,"E74.MirrorCS");var subQ1=sQuery(id+"F2.wireOp",EDGE,"E21.0");var subQ2=makeQuery(id+"F2.imprint","INTERSECT",VERTEX,{"derivedFrom":[subQ1,subQ0]});Q135=makeQuery(id+"F2.imprint","IMPRINT",FACE,{"disambiguationData":[TD([[makeQuery(id+"F2.imprint","IMPRINT",EDGE,{"disambiguationData":[TD([[subQ2,-1.0]])],"derivedFrom":subQ1}),-1.0]])]});}
            var Q136;
            {var subQ0=sQuery(id+"F2.wireOp",EDGE,"E72.MirrorCS");var subQ1=sQuery(id+"F2.wireOp",EDGE,"E21.0");var subQ2=makeQuery(id+"F2.imprint","INTERSECT",VERTEX,{"derivedFrom":[subQ1,subQ0]});Q136=makeQuery(id+"F2.imprint","IMPRINT",FACE,{"disambiguationData":[TD([[makeQuery(id+"F2.imprint","IMPRINT",EDGE,{"disambiguationData":[TD([[subQ2,-1.0]])],"derivedFrom":subQ1}),-1.0]])]});}
            var Q137;
            {var subQ0=sQuery(id+"F2.wireOp",EDGE,"E70.MirrorCS");var subQ1=sQuery(id+"F2.wireOp",EDGE,"E21.0");var subQ2=makeQuery(id+"F2.imprint","INTERSECT",VERTEX,{"derivedFrom":[subQ1,subQ0]});Q137=makeQuery(id+"F2.imprint","IMPRINT",FACE,{"disambiguationData":[TD([[makeQuery(id+"F2.imprint","IMPRINT",EDGE,{"disambiguationData":[TD([[subQ2,-1.0]])],"derivedFrom":subQ1}),-1.0]])]});}
            var Q138;
            {var subQ0=sQuery(id+"F2.wireOp",EDGE,"E77.MirrorCS");var subQ1=sQuery(id+"F2.wireOp",EDGE,"E21.0");var subQ2=makeQuery(id+"F2.imprint","INTERSECT",VERTEX,{"derivedFrom":[subQ1,subQ0]});Q138=makeQuery(id+"F2.imprint","IMPRINT",FACE,{"disambiguationData":[TD([[makeQuery(id+"F2.imprint","IMPRINT",EDGE,{"disambiguationData":[TD([[subQ2,-1.0]])],"derivedFrom":subQ1}),-1.0]])]});}
            var Q139;
            {var subQ0=sQuery(id+"F2.wireOp",EDGE,"E66.MirrorCS");var subQ1=sQuery(id+"F2.wireOp",EDGE,"E21.0");var subQ2=makeQuery(id+"F2.imprint","INTERSECT",VERTEX,{"derivedFrom":[subQ1,subQ0]});Q139=makeQuery(id+"F2.imprint","IMPRINT",FACE,{"disambiguationData":[TD([[makeQuery(id+"F2.imprint","IMPRINT",EDGE,{"disambiguationData":[TD([[subQ2,-1.0]])],"derivedFrom":subQ1}),-1.0]])]});}
            var Q140;
            {var subQ0=sQuery(id+"F2.wireOp",EDGE,"E69.MirrorCS");var subQ1=sQuery(id+"F2.wireOp",EDGE,"E21.0");var subQ2=makeQuery(id+"F2.imprint","INTERSECT",VERTEX,{"derivedFrom":[subQ1,subQ0]});Q140=makeQuery(id+"F2.imprint","IMPRINT",FACE,{"disambiguationData":[TD([[makeQuery(id+"F2.imprint","IMPRINT",EDGE,{"disambiguationData":[TD([[subQ2,-1.0]])],"derivedFrom":subQ1}),-1.0]])]});}
            var Q141;
            {var subQ0=sQuery(id+"F2.wireOp",EDGE,"E65.MirrorCS");var subQ1=sQuery(id+"F2.wireOp",EDGE,"E21.0");var subQ2=makeQuery(id+"F2.imprint","INTERSECT",VERTEX,{"derivedFrom":[subQ1,subQ0]});Q141=makeQuery(id+"F2.imprint","IMPRINT",FACE,{"disambiguationData":[TD([[makeQuery(id+"F2.imprint","IMPRINT",EDGE,{"disambiguationData":[TD([[subQ2,-1.0]])],"derivedFrom":subQ1}),-1.0]])]});}
            var Q142;
            {var subQ0=sQuery(id+"F2.wireOp",EDGE,"E78.MirrorCS");var subQ1=sQuery(id+"F2.wireOp",EDGE,"E21.0");var subQ2=makeQuery(id+"F2.imprint","INTERSECT",VERTEX,{"derivedFrom":[subQ1,subQ0]});Q142=makeQuery(id+"F2.imprint","IMPRINT",FACE,{"disambiguationData":[TD([[makeQuery(id+"F2.imprint","IMPRINT",EDGE,{"disambiguationData":[TD([[subQ2,-1.0]])],"derivedFrom":subQ1}),-1.0]])]});}
            var Q143;
            {var subQ0=sQuery(id+"F2.wireOp",EDGE,"E78.MirrorCS");var subQ1=sQuery(id+"F2.wireOp",EDGE,"E23.0");var subQ2=makeQuery(id+"F2.imprint","INTERSECT",VERTEX,{"derivedFrom":[subQ1,subQ0]});Q143=makeQuery(id+"F2.imprint","IMPRINT",FACE,{"disambiguationData":[TD([[makeQuery(id+"F2.imprint","IMPRINT",EDGE,{"disambiguationData":[TD([[subQ2,-1.0]])],"derivedFrom":subQ1}),-1.0]])]});}
            var Q144;
            {var subQ0=sQuery(id+"F2.wireOp",EDGE,"E80.MirrorCS");var subQ1=sQuery(id+"F2.wireOp",EDGE,"E23.0");var subQ2=makeQuery(id+"F2.imprint","INTERSECT",VERTEX,{"derivedFrom":[subQ1,subQ0]});Q144=makeQuery(id+"F2.imprint","IMPRINT",FACE,{"disambiguationData":[TD([[makeQuery(id+"F2.imprint","IMPRINT",EDGE,{"disambiguationData":[TD([[subQ2,-1.0]])],"derivedFrom":subQ1}),-1.0]])]});}
            var Q145;
            {var subQ0=sQuery(id+"F2.wireOp",EDGE,"E82.MirrorCS");var subQ1=sQuery(id+"F2.wireOp",EDGE,"E23.0");var subQ2=makeQuery(id+"F2.imprint","INTERSECT",VERTEX,{"derivedFrom":[subQ1,subQ0]});Q145=makeQuery(id+"F2.imprint","IMPRINT",FACE,{"disambiguationData":[TD([[makeQuery(id+"F2.imprint","IMPRINT",EDGE,{"disambiguationData":[TD([[subQ2,-1.0]])],"derivedFrom":subQ1}),-1.0]])]});}
            var Q146;
            {var subQ0=sQuery(id+"F2.wireOp",EDGE,"E84.MirrorCS");var subQ1=sQuery(id+"F2.wireOp",EDGE,"E23.0");var subQ2=makeQuery(id+"F2.imprint","INTERSECT",VERTEX,{"derivedFrom":[subQ1,subQ0]});Q146=makeQuery(id+"F2.imprint","IMPRINT",FACE,{"disambiguationData":[TD([[makeQuery(id+"F2.imprint","IMPRINT",EDGE,{"disambiguationData":[TD([[subQ2,-1.0]])],"derivedFrom":subQ1}),-1.0]])]});}
            var Q147;
            {var subQ0=sQuery(id+"F2.wireOp",EDGE,"E23.0");var subQ1=sQuery(id+"F2.wireOp",EDGE,"E1.MirrorCS");var subQ2=makeQuery(id+"F2.imprint","INTERSECT",VERTEX,{"derivedFrom":[subQ1,subQ0]});Q147=makeQuery(id+"F2.imprint","IMPRINT",FACE,{"disambiguationData":[TD([[makeQuery(id+"F2.imprint","IMPRINT",EDGE,{"disambiguationData":[TD([[subQ2,-1.0]])],"derivedFrom":subQ1}),1.0]])]});}
            var Q148;
            {var subQ0=sQuery(id+"F2.wireOp",EDGE,"E23.0");var subQ1=sQuery(id+"F2.wireOp",EDGE,"E2");var subQ2=makeQuery(id+"F2.imprint","INTERSECT",VERTEX,{"derivedFrom":[subQ1,subQ0]});Q148=makeQuery(id+"F2.imprint","IMPRINT",FACE,{"disambiguationData":[TD([[makeQuery(id+"F2.imprint","IMPRINT",EDGE,{"disambiguationData":[TD([[subQ2,1.0]])],"derivedFrom":subQ1}),-1.0]])]});}
            var Q149;
            {var subQ0=sQuery(id+"F2.wireOp",EDGE,"E25.0");var subQ1=sQuery(id+"F2.wireOp",EDGE,"E2");var subQ2=makeQuery(id+"F2.imprint","INTERSECT",VERTEX,{"derivedFrom":[subQ1,subQ0]});Q149=makeQuery(id+"F2.imprint","IMPRINT",FACE,{"disambiguationData":[TD([[makeQuery(id+"F2.imprint","IMPRINT",EDGE,{"disambiguationData":[TD([[subQ2,1.0]])],"derivedFrom":subQ1}),-1.0]])]});}
            var Q150;
            {var subQ0=sQuery(id+"F2.wireOp",EDGE,"E25.0");var subQ1=sQuery(id+"F2.wireOp",EDGE,"E1.MirrorCS");var subQ2=makeQuery(id+"F2.imprint","INTERSECT",VERTEX,{"derivedFrom":[subQ1,subQ0]});Q150=makeQuery(id+"F2.imprint","IMPRINT",FACE,{"disambiguationData":[TD([[makeQuery(id+"F2.imprint","IMPRINT",EDGE,{"disambiguationData":[TD([[subQ2,-1.0]])],"derivedFrom":subQ1}),1.0]])]});}
            var Q151;
            {var subQ0=sQuery(id+"F2.wireOp",EDGE,"E84.MirrorCS");var subQ1=sQuery(id+"F2.wireOp",EDGE,"E25.0");var subQ2=makeQuery(id+"F2.imprint","INTERSECT",VERTEX,{"derivedFrom":[subQ1,subQ0]});Q151=makeQuery(id+"F2.imprint","IMPRINT",FACE,{"disambiguationData":[TD([[makeQuery(id+"F2.imprint","IMPRINT",EDGE,{"disambiguationData":[TD([[subQ2,-1.0]])],"derivedFrom":subQ1}),-1.0]])]});}
            var Q152;
            {var subQ0=sQuery(id+"F2.wireOp",EDGE,"E82.MirrorCS");var subQ1=sQuery(id+"F2.wireOp",EDGE,"E25.0");var subQ2=makeQuery(id+"F2.imprint","INTERSECT",VERTEX,{"derivedFrom":[subQ1,subQ0]});Q152=makeQuery(id+"F2.imprint","IMPRINT",FACE,{"disambiguationData":[TD([[makeQuery(id+"F2.imprint","IMPRINT",EDGE,{"disambiguationData":[TD([[subQ2,-1.0]])],"derivedFrom":subQ1}),-1.0]])]});}
            var Q153;
            {var subQ0=sQuery(id+"F2.wireOp",EDGE,"E80.MirrorCS");var subQ1=sQuery(id+"F2.wireOp",EDGE,"E25.0");var subQ2=makeQuery(id+"F2.imprint","INTERSECT",VERTEX,{"derivedFrom":[subQ1,subQ0]});Q153=makeQuery(id+"F2.imprint","IMPRINT",FACE,{"disambiguationData":[TD([[makeQuery(id+"F2.imprint","IMPRINT",EDGE,{"disambiguationData":[TD([[subQ2,-1.0]])],"derivedFrom":subQ1}),-1.0]])]});}
            var Q154;
            {var subQ0=sQuery(id+"F2.wireOp",EDGE,"E78.MirrorCS");var subQ1=sQuery(id+"F2.wireOp",EDGE,"E25.0");var subQ2=makeQuery(id+"F2.imprint","INTERSECT",VERTEX,{"derivedFrom":[subQ1,subQ0]});Q154=makeQuery(id+"F2.imprint","IMPRINT",FACE,{"disambiguationData":[TD([[makeQuery(id+"F2.imprint","IMPRINT",EDGE,{"disambiguationData":[TD([[subQ2,-1.0]])],"derivedFrom":subQ1}),-1.0]])]});}
            var Q155;
            {var subQ0=sQuery(id+"F2.wireOp",EDGE,"E88.MirrorCS");var subQ1=sQuery(id+"F2.wireOp",EDGE,"E25.0");var subQ2=makeQuery(id+"F2.imprint","INTERSECT",VERTEX,{"derivedFrom":[subQ1,subQ0]});Q155=makeQuery(id+"F2.imprint","IMPRINT",FACE,{"disambiguationData":[TD([[makeQuery(id+"F2.imprint","IMPRINT",EDGE,{"disambiguationData":[TD([[subQ2,-1.0]])],"derivedFrom":subQ1}),-1.0]])]});}
            var Q156;
            {var subQ0=sQuery(id+"F2.wireOp",EDGE,"E88.MirrorCS");var subQ1=sQuery(id+"F2.wireOp",EDGE,"E23.0");var subQ2=makeQuery(id+"F2.imprint","INTERSECT",VERTEX,{"derivedFrom":[subQ1,subQ0]});Q156=makeQuery(id+"F2.imprint","IMPRINT",FACE,{"disambiguationData":[TD([[makeQuery(id+"F2.imprint","IMPRINT",EDGE,{"disambiguationData":[TD([[subQ2,-1.0]])],"derivedFrom":subQ1}),-1.0]])]});}
            var Q157;
            {var subQ0=sQuery(id+"F2.wireOp",EDGE,"E74.MirrorCS");var subQ1=sQuery(id+"F2.wireOp",EDGE,"E25.0");var subQ2=makeQuery(id+"F2.imprint","INTERSECT",VERTEX,{"derivedFrom":[subQ1,subQ0]});Q157=makeQuery(id+"F2.imprint","IMPRINT",FACE,{"disambiguationData":[TD([[makeQuery(id+"F2.imprint","IMPRINT",EDGE,{"disambiguationData":[TD([[subQ2,-1.0]])],"derivedFrom":subQ1}),-1.0]])]});}
            var Q158;
            {var subQ0=sQuery(id+"F2.wireOp",EDGE,"E72.MirrorCS");var subQ1=sQuery(id+"F2.wireOp",EDGE,"E25.0");var subQ2=makeQuery(id+"F2.imprint","INTERSECT",VERTEX,{"derivedFrom":[subQ1,subQ0]});Q158=makeQuery(id+"F2.imprint","IMPRINT",FACE,{"disambiguationData":[TD([[makeQuery(id+"F2.imprint","IMPRINT",EDGE,{"disambiguationData":[TD([[subQ2,-1.0]])],"derivedFrom":subQ1}),-1.0]])]});}
            var Q159;
            {var subQ0=sQuery(id+"F2.wireOp",EDGE,"E72.MirrorCS");var subQ1=sQuery(id+"F2.wireOp",EDGE,"E23.0");var subQ2=makeQuery(id+"F2.imprint","INTERSECT",VERTEX,{"derivedFrom":[subQ1,subQ0]});Q159=makeQuery(id+"F2.imprint","IMPRINT",FACE,{"disambiguationData":[TD([[makeQuery(id+"F2.imprint","IMPRINT",EDGE,{"disambiguationData":[TD([[subQ2,-1.0]])],"derivedFrom":subQ1}),-1.0]])]});}
            var Q160;
            {var subQ0=sQuery(id+"F2.wireOp",EDGE,"E74.MirrorCS");var subQ1=sQuery(id+"F2.wireOp",EDGE,"E23.0");var subQ2=makeQuery(id+"F2.imprint","INTERSECT",VERTEX,{"derivedFrom":[subQ1,subQ0]});Q160=makeQuery(id+"F2.imprint","IMPRINT",FACE,{"disambiguationData":[TD([[makeQuery(id+"F2.imprint","IMPRINT",EDGE,{"disambiguationData":[TD([[subQ2,-1.0]])],"derivedFrom":subQ1}),-1.0]])]});}
            var Q161;
            {var subQ0=sQuery(id+"F2.wireOp",EDGE,"E70.MirrorCS");var subQ1=sQuery(id+"F2.wireOp",EDGE,"E23.0");var subQ2=makeQuery(id+"F2.imprint","INTERSECT",VERTEX,{"derivedFrom":[subQ1,subQ0]});Q161=makeQuery(id+"F2.imprint","IMPRINT",FACE,{"disambiguationData":[TD([[makeQuery(id+"F2.imprint","IMPRINT",EDGE,{"disambiguationData":[TD([[subQ2,-1.0]])],"derivedFrom":subQ1}),-1.0]])]});}
            var Q162;
            {var subQ0=sQuery(id+"F2.wireOp",EDGE,"E77.MirrorCS");var subQ1=sQuery(id+"F2.wireOp",EDGE,"E25.0");var subQ2=makeQuery(id+"F2.imprint","INTERSECT",VERTEX,{"derivedFrom":[subQ1,subQ0]});Q162=makeQuery(id+"F2.imprint","IMPRINT",FACE,{"disambiguationData":[TD([[makeQuery(id+"F2.imprint","IMPRINT",EDGE,{"disambiguationData":[TD([[subQ2,-1.0]])],"derivedFrom":subQ1}),-1.0]])]});}
            var Q163;
            {var subQ0=sQuery(id+"F2.wireOp",EDGE,"E77.MirrorCS");var subQ1=sQuery(id+"F2.wireOp",EDGE,"E23.0");var subQ2=makeQuery(id+"F2.imprint","INTERSECT",VERTEX,{"derivedFrom":[subQ1,subQ0]});Q163=makeQuery(id+"F2.imprint","IMPRINT",FACE,{"disambiguationData":[TD([[makeQuery(id+"F2.imprint","IMPRINT",EDGE,{"disambiguationData":[TD([[subQ2,-1.0]])],"derivedFrom":subQ1}),-1.0]])]});}
            var Q164;
            {var subQ0=sQuery(id+"F2.wireOp",EDGE,"E66.MirrorCS");var subQ1=sQuery(id+"F2.wireOp",EDGE,"E23.0");var subQ2=makeQuery(id+"F2.imprint","INTERSECT",VERTEX,{"derivedFrom":[subQ1,subQ0]});Q164=makeQuery(id+"F2.imprint","IMPRINT",FACE,{"disambiguationData":[TD([[makeQuery(id+"F2.imprint","IMPRINT",EDGE,{"disambiguationData":[TD([[subQ2,-1.0]])],"derivedFrom":subQ1}),-1.0]])]});}
            var Q165;
            {var subQ0=sQuery(id+"F2.wireOp",EDGE,"E66.MirrorCS");var subQ1=sQuery(id+"F2.wireOp",EDGE,"E25.0");var subQ2=makeQuery(id+"F2.imprint","INTERSECT",VERTEX,{"derivedFrom":[subQ1,subQ0]});Q165=makeQuery(id+"F2.imprint","IMPRINT",FACE,{"disambiguationData":[TD([[makeQuery(id+"F2.imprint","IMPRINT",EDGE,{"disambiguationData":[TD([[subQ2,-1.0]])],"derivedFrom":subQ1}),-1.0]])]});}
            var Q166;
            {var subQ0=sQuery(id+"F2.wireOp",EDGE,"E69.MirrorCS");var subQ1=sQuery(id+"F2.wireOp",EDGE,"E23.0");var subQ2=makeQuery(id+"F2.imprint","INTERSECT",VERTEX,{"derivedFrom":[subQ1,subQ0]});Q166=makeQuery(id+"F2.imprint","IMPRINT",FACE,{"disambiguationData":[TD([[makeQuery(id+"F2.imprint","IMPRINT",EDGE,{"disambiguationData":[TD([[subQ2,-1.0]])],"derivedFrom":subQ1}),-1.0]])]});}
            var Q167;
            {var subQ0=sQuery(id+"F2.wireOp",EDGE,"E65.MirrorCS");var subQ1=sQuery(id+"F2.wireOp",EDGE,"E23.0");var subQ2=makeQuery(id+"F2.imprint","INTERSECT",VERTEX,{"derivedFrom":[subQ1,subQ0]});Q167=makeQuery(id+"F2.imprint","IMPRINT",FACE,{"disambiguationData":[TD([[makeQuery(id+"F2.imprint","IMPRINT",EDGE,{"disambiguationData":[TD([[subQ2,-1.0]])],"derivedFrom":subQ1}),-1.0]])]});}
            var Q168;
            {var subQ0=sQuery(id+"F2.wireOp",EDGE,"E65.MirrorCS");var subQ1=sQuery(id+"F2.wireOp",EDGE,"E25.0");var subQ2=makeQuery(id+"F2.imprint","INTERSECT",VERTEX,{"derivedFrom":[subQ1,subQ0]});Q168=makeQuery(id+"F2.imprint","IMPRINT",FACE,{"disambiguationData":[TD([[makeQuery(id+"F2.imprint","IMPRINT",EDGE,{"disambiguationData":[TD([[subQ2,-1.0]])],"derivedFrom":subQ1}),-1.0]])]});}
            extrude(context, id + "F3", {"entities" : qUnion([Q0, Q1, Q2, Q3, Q4, Q5, Q6, Q7, Q8, Q9, Q10, Q11, Q12, Q13, Q14, Q15, Q16, Q17, Q18, Q19, Q20, Q21, Q22, Q23, Q24, Q25, Q26, Q27, Q28, Q29, Q30, Q31, Q32, Q33, Q34, Q35, Q36, Q37, Q38, Q39, Q40, Q41, Q42, Q43, Q44, Q45, Q46, Q47, Q48, Q49, Q50, Q51, Q52, Q53, Q54, Q55, Q56, Q57, Q58, Q59, Q60, Q61, Q62, Q63, Q64, Q65, Q66, Q67, Q68, Q69, Q70, Q71, Q72, Q73, Q74, Q75, Q76, Q77, Q78, Q79, Q80, Q81, Q82, Q83, Q84, Q85, Q86, Q87, Q88, Q89, Q90, Q91, Q92, Q93, Q94, Q95, Q96, Q97, Q98, Q99, Q100, Q101, Q102, Q103, Q104, Q105, Q106, Q107, Q108, Q109, Q110, Q111, Q112, Q113, Q114, Q115, Q116, Q117, Q118, Q119, Q120, Q121, Q122, Q123, Q124, Q125, Q126, Q127, Q128, Q129, Q130, Q131, Q132, Q133, Q134, Q135, Q136, Q137, Q138, Q139, Q140, Q141, Q142, Q143, Q144, Q145, Q146, Q147, Q148, Q149, Q150, Q151, Q152, Q153, Q154, Q155, Q156, Q157, Q158, Q159, Q160, Q161, Q162, Q163, Q164, Q165, Q166, Q167, Q168]), "operationType" : NewBodyOperationType.ADD, "oppositeDirection" : true, "depth" : 300 * mm});
        }
    });
